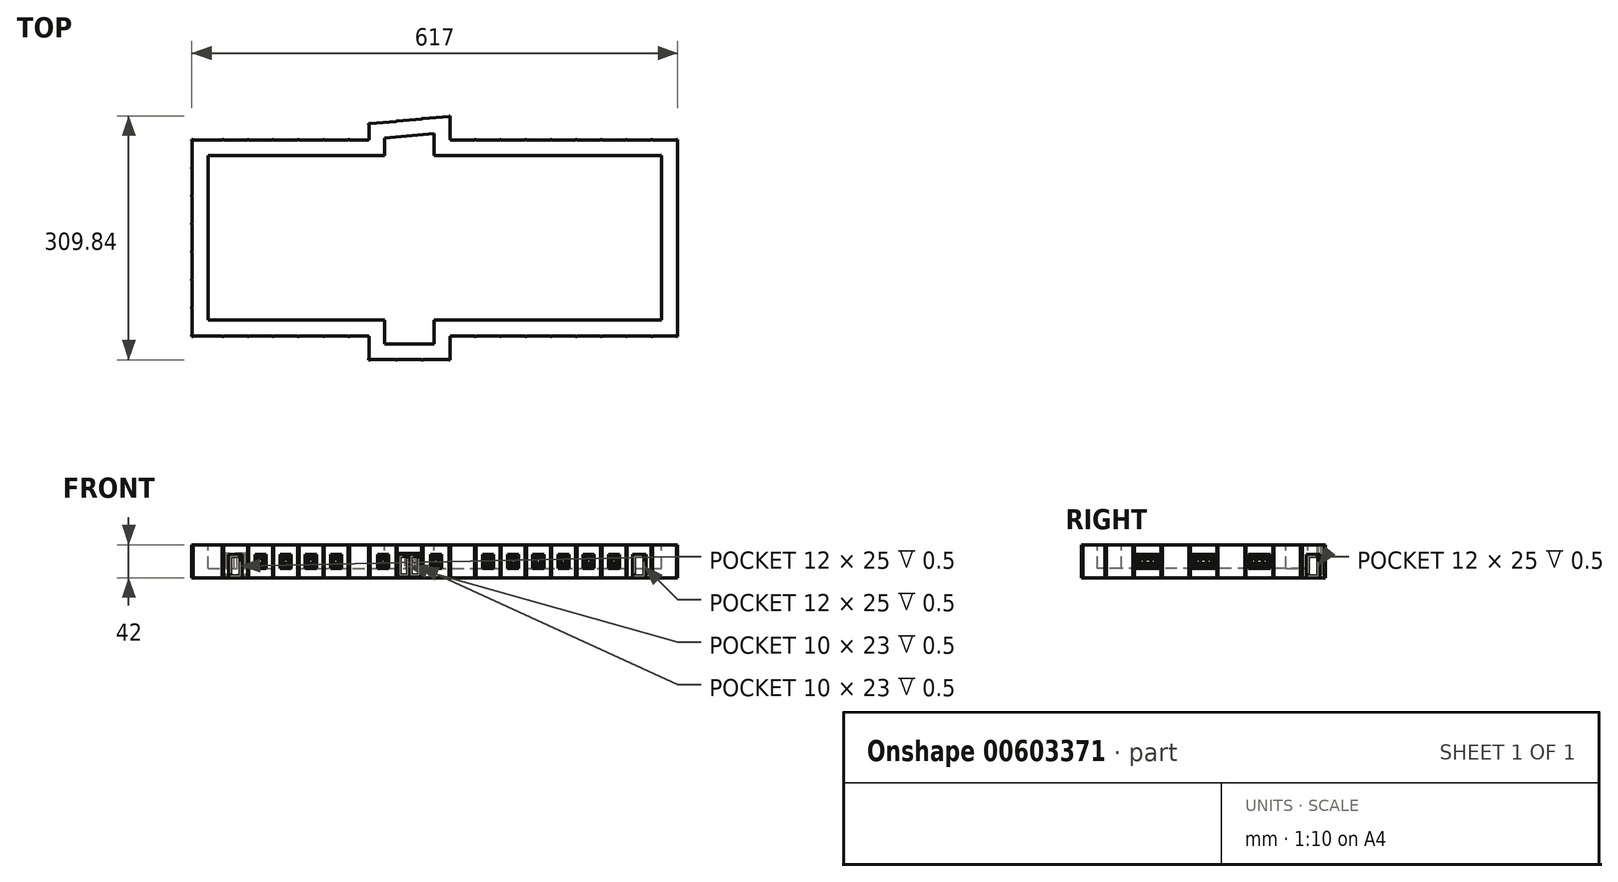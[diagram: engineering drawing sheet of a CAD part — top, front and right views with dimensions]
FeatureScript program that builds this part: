
annotation { "Feature Type Name" : "Feature", "Feature Type Description" : "" }
export const myFeature = defineFeature(function(context is Context, id is Id, definition is map)
    precondition{}
    {
        {
            var Q0;
            Q0=qCreatedBy(makeId("Top.planeOp"),FACE);
            var sketch = newSketch(context, id + "F0", { "sketchPlane" : qUnion([Q0])});
            skLineSegment(sketch, "E0", {"start": v(-327.3, -140.86) * mm, "end": v(-102.6, -140.86) * mm});
            skLineSegment(sketch, "E1", {"start": v(-102.6, -140.86) * mm, "end": v(-102.6, -170.86) * mm});
            skLineSegment(sketch, "E2", {"start": v(-102.6, -170.86) * mm, "end": v(0, -170.86) * mm});
            skLineSegment(sketch, "E3", {"start": v(0, -170.86) * mm, "end": v(0, -140.86) * mm});
            skLineSegment(sketch, "E4", {"start": v(0, -140.86) * mm, "end": v(288.9, -140.86) * mm});
            skLineSegment(sketch, "E5", {"start": v(288.9, -140.86) * mm, "end": v(288.9, 108.14) * mm});
            skLineSegment(sketch, "E6", {"start": v(288.9, 108.14) * mm, "end": v(0, 108.14) * mm});
            skLineSegment(sketch, "E7", {"start": v(0, 108.14) * mm, "end": v(0, 138.14) * mm});
            skLineSegment(sketch, "E8", {"start": v(-102.6, 128.64) * mm, "end": v(-102.6, 108.14) * mm});
            skLineSegment(sketch, "E9", {"start": v(-102.6, 108.14) * mm, "end": v(-327.3, 108.14) * mm});
            skLineSegment(sketch, "E10", {"start": v(-327.3, 108.14) * mm, "end": v(-327.3, -140.86) * mm});
            skLineSegment(sketch, "E11", {"start": v(-102.6, 128.64) * mm, "end": v(0, 138.14) * mm});
            skSolve(sketch);
        }
        {
            var Q0;
            Q0=makeQuery(id+"F0.imprint","IMPRINT",FACE,{"disambiguationData":[TD([[makeQuery(id+"F0.imprint","IMPRINT",EDGE,{"derivedFrom":sQuery(id+"F0.wireOp",EDGE,"E0")}),1.0]])]});
            extrude(context, id + "F1", {"entities" : qUnion([Q0]), "depth" : 42 * mm, "offsetDistance" : 25 * mm});
        }
        {
            var Q0;
            Q0=makeQuery(id+"F19.boolean.opBoolean","MERGE",FACE,{"derivedFrom":[makeQuery(id+"F18.boolean.opBoolean","MERGE",FACE,{"derivedFrom":[makeQuery(id+"F17.boolean.opBoolean","MERGE",FACE,{"derivedFrom":[makeQuery(id+"F16.boolean.opBoolean","MERGE",FACE,{"derivedFrom":[makeQuery(id+"F1.opExtrude","CAP_FACE",FACE,{"disambiguationData":[OSD([sQuery(id+"F0.wireOp",EDGE,"E0"),sQuery(id+"F0.wireOp",EDGE,"E1"),sQuery(id+"F0.wireOp",EDGE,"E2"),sQuery(id+"F0.wireOp",EDGE,"E3"),sQuery(id+"F0.wireOp",EDGE,"E4"),sQuery(id+"F0.wireOp",EDGE,"E5"),sQuery(id+"F0.wireOp",EDGE,"E6"),sQuery(id+"F0.wireOp",EDGE,"E7"),sQuery(id+"F0.wireOp",EDGE,"E8"),sQuery(id+"F0.wireOp",EDGE,"E9"),sQuery(id+"F0.wireOp",EDGE,"E10"),sQuery(id+"F0.wireOp",EDGE,"E11")])],"isStart":false}),makeQuery(id+"F16.opExtrude","SWEPT_FACE",FACE,{"disambiguationData":[OSD([sQuery(id+"F4.wireOp",EDGE,"E25.bottom")])]}),makeQuery(id+"F16.opExtrude","SWEPT_FACE",FACE,{"disambiguationData":[OSD([sQuery(id+"F4.wireOp",EDGE,"E26.bottom")])]}),makeQuery(id+"F16.opExtrude","SWEPT_FACE",FACE,{"disambiguationData":[OSD([sQuery(id+"F4.wireOp",EDGE,"E27.bottom")])]}),makeQuery(id+"F16.opExtrude","SWEPT_FACE",FACE,{"disambiguationData":[OSD([sQuery(id+"F4.wireOp",EDGE,"E28.bottom")])]}),makeQuery(id+"F16.opExtrude","SWEPT_FACE",FACE,{"disambiguationData":[OSD([sQuery(id+"F4.wireOp",EDGE,"E29.bottom")])]}),makeQuery(id+"F16.opExtrude","SWEPT_FACE",FACE,{"disambiguationData":[OSD([sQuery(id+"F4.wireOp",EDGE,"E30.bottom")])]}),makeQuery(id+"F16.opExtrude","SWEPT_FACE",FACE,{"disambiguationData":[OSD([sQuery(id+"F4.wireOp",EDGE,"E31.bottom")])]}),makeQuery(id+"F16.opExtrude","SWEPT_FACE",FACE,{"disambiguationData":[OSD([sQuery(id+"F4.wireOp",EDGE,"E33.bottom")])]}),makeQuery(id+"F16.opExtrude","SWEPT_FACE",FACE,{"disambiguationData":[OSD([sQuery(id+"F6.wireOp",EDGE,"E39.bottom")])]}),makeQuery(id+"F16.opExtrude","SWEPT_FACE",FACE,{"disambiguationData":[OSD([sQuery(id+"F6.wireOp",EDGE,"E40.bottom")])]}),makeQuery(id+"F16.opExtrude","SWEPT_FACE",FACE,{"disambiguationData":[OSD([sQuery(id+"F6.wireOp",EDGE,"E46.bottom")])]}),makeQuery(id+"F16.opExtrude","SWEPT_FACE",FACE,{"disambiguationData":[OSD([sQuery(id+"F6.wireOp",EDGE,"E47.bottom")])]}),makeQuery(id+"F16.opExtrude","SWEPT_FACE",FACE,{"disambiguationData":[OSD([sQuery(id+"F8.wireOp",EDGE,"E52.bottom")])]}),makeQuery(id+"F16.opExtrude","SWEPT_FACE",FACE,{"disambiguationData":[OSD([sQuery(id+"F8.wireOp",EDGE,"E62.bottom")])]}),makeQuery(id+"F16.opExtrude","SWEPT_FACE",FACE,{"disambiguationData":[OSD([sQuery(id+"F8.wireOp",EDGE,"E63.1.0.1")])]}),makeQuery(id+"F16.opExtrude","SWEPT_FACE",FACE,{"disambiguationData":[OSD([sQuery(id+"F8.wireOp",EDGE,"E63.2.0.1")])]}),makeQuery(id+"F16.opExtrude","SWEPT_FACE",FACE,{"disambiguationData":[OSD([sQuery(id+"F8.wireOp",EDGE,"E63.3.0.1")])]}),makeQuery(id+"F16.opExtrude","SWEPT_FACE",FACE,{"disambiguationData":[OSD([sQuery(id+"F8.wireOp",EDGE,"E63.4.0.1")])]}),makeQuery(id+"F16.opExtrude","SWEPT_FACE",FACE,{"disambiguationData":[OSD([sQuery(id+"F8.wireOp",EDGE,"E63.5.0.1")])]}),makeQuery(id+"F16.opExtrude","SWEPT_FACE",FACE,{"disambiguationData":[OSD([sQuery(id+"F8.wireOp",EDGE,"E63.6.0.1")])]}),makeQuery(id+"F16.opExtrude","SWEPT_FACE",FACE,{"disambiguationData":[OSD([sQuery(id+"F8.wireOp",EDGE,"E63.7.0.1")])]}),makeQuery(id+"F16.opExtrude","SWEPT_FACE",FACE,{"disambiguationData":[OSD([sQuery(id+"F8.wireOp",EDGE,"E64.bottom")])]})]}),makeQuery(id+"F17.opExtrude","SWEPT_FACE",FACE,{"disambiguationData":[OSD([sQuery(id+"F5.wireOp",EDGE,"E34.bottom")])]}),makeQuery(id+"F17.opExtrude","SWEPT_FACE",FACE,{"disambiguationData":[OSD([sQuery(id+"F5.wireOp",EDGE,"E36.bottom")])]}),makeQuery(id+"F17.opExtrude","SWEPT_FACE",FACE,{"disambiguationData":[OSD([sQuery(id+"F10.wireOp",EDGE,"E70.bottom")])]}),makeQuery(id+"F17.opExtrude","SWEPT_FACE",FACE,{"disambiguationData":[OSD([sQuery(id+"F10.wireOp",EDGE,"E71.1.0.1")])]}),makeQuery(id+"F17.opExtrude","SWEPT_FACE",FACE,{"disambiguationData":[OSD([sQuery(id+"F10.wireOp",EDGE,"E71.2.0.1")])]}),makeQuery(id+"F17.opExtrude","SWEPT_FACE",FACE,{"disambiguationData":[OSD([sQuery(id+"F10.wireOp",EDGE,"E71.3.0.1")])]}),makeQuery(id+"F17.opExtrude","SWEPT_FACE",FACE,{"disambiguationData":[OSD([sQuery(id+"F10.wireOp",EDGE,"E71.4.0.1")])]}),makeQuery(id+"F17.opExtrude","SWEPT_FACE",FACE,{"disambiguationData":[OSD([sQuery(id+"F10.wireOp",EDGE,"E71.5.0.1")])]}),makeQuery(id+"F17.opExtrude","SWEPT_FACE",FACE,{"disambiguationData":[OSD([sQuery(id+"F10.wireOp",EDGE,"E71.6.0.1")])]}),makeQuery(id+"F17.opExtrude","SWEPT_FACE",FACE,{"disambiguationData":[OSD([sQuery(id+"F10.wireOp",EDGE,"E71.7.0.1")])]}),makeQuery(id+"F17.opExtrude","SWEPT_FACE",FACE,{"disambiguationData":[OSD([sQuery(id+"F10.wireOp",EDGE,"E71.8.0.1")])]}),makeQuery(id+"F17.opExtrude","SWEPT_FACE",FACE,{"disambiguationData":[OSD([sQuery(id+"F12.wireOp",EDGE,"E93.bottom")])]}),makeQuery(id+"F17.opExtrude","SWEPT_FACE",FACE,{"disambiguationData":[OSD([sQuery(id+"F12.wireOp",EDGE,"E95.bottom")])]})]}),makeQuery(id+"F18.opExtrude","SWEPT_FACE",FACE,{"disambiguationData":[OSD([sQuery(id+"F7.wireOp",EDGE,"E48.bottom")])]}),makeQuery(id+"F18.opExtrude","SWEPT_FACE",FACE,{"disambiguationData":[OSD([sQuery(id+"F7.wireOp",EDGE,"E50.bottom")])]}),makeQuery(id+"F18.opExtrude","SWEPT_FACE",FACE,{"disambiguationData":[OSD([sQuery(id+"F9.wireOp",EDGE,"E66.bottom")])]}),makeQuery(id+"F18.opExtrude","SWEPT_FACE",FACE,{"disambiguationData":[OSD([sQuery(id+"F9.wireOp",EDGE,"E67.1.0.1")])]}),makeQuery(id+"F18.opExtrude","SWEPT_FACE",FACE,{"disambiguationData":[OSD([sQuery(id+"F9.wireOp",EDGE,"E67.2.0.1")])]}),makeQuery(id+"F18.opExtrude","SWEPT_FACE",FACE,{"disambiguationData":[OSD([sQuery(id+"F9.wireOp",EDGE,"E67.3.0.1")])]}),makeQuery(id+"F18.opExtrude","SWEPT_FACE",FACE,{"disambiguationData":[OSD([sQuery(id+"F9.wireOp",EDGE,"E67.4.0.1")])]}),makeQuery(id+"F18.opExtrude","SWEPT_FACE",FACE,{"disambiguationData":[OSD([sQuery(id+"F9.wireOp",EDGE,"E67.5.0.1")])]}),makeQuery(id+"F18.opExtrude","SWEPT_FACE",FACE,{"disambiguationData":[OSD([sQuery(id+"F9.wireOp",EDGE,"E67.6.0.1")])]}),makeQuery(id+"F18.opExtrude","SWEPT_FACE",FACE,{"disambiguationData":[OSD([sQuery(id+"F9.wireOp",EDGE,"E67.7.0.1")])]}),makeQuery(id+"F18.opExtrude","SWEPT_FACE",FACE,{"disambiguationData":[OSD([sQuery(id+"F9.wireOp",EDGE,"E67.8.0.1")])]}),makeQuery(id+"F18.opExtrude","SWEPT_FACE",FACE,{"disambiguationData":[OSD([sQuery(id+"F14.wireOp",EDGE,"E107.bottom")])]}),makeQuery(id+"F18.opExtrude","SWEPT_FACE",FACE,{"disambiguationData":[OSD([sQuery(id+"F14.wireOp",EDGE,"E109.bottom")])]})]}),makeQuery(id+"F19.opExtrude","SWEPT_FACE",FACE,{"disambiguationData":[OSD([sQuery(id+"F11.wireOp",EDGE,"E84.top")])]}),makeQuery(id+"F19.opExtrude","SWEPT_FACE",FACE,{"disambiguationData":[OSD([sQuery(id+"F11.wireOp",EDGE,"E85.top")])]}),makeQuery(id+"F19.opExtrude","SWEPT_FACE",FACE,{"disambiguationData":[OSD([sQuery(id+"F11.wireOp",EDGE,"E86.top")])]}),makeQuery(id+"F19.opExtrude","SWEPT_FACE",FACE,{"disambiguationData":[OSD([sQuery(id+"F11.wireOp",EDGE,"E87.top")])]}),makeQuery(id+"F19.opExtrude","SWEPT_FACE",FACE,{"disambiguationData":[OSD([sQuery(id+"F11.wireOp",EDGE,"E88.top")])]}),makeQuery(id+"F19.opExtrude","SWEPT_FACE",FACE,{"disambiguationData":[OSD([sQuery(id+"F11.wireOp",EDGE,"E89.top")])]}),makeQuery(id+"F19.opExtrude","SWEPT_FACE",FACE,{"disambiguationData":[OSD([sQuery(id+"F11.wireOp",EDGE,"E90.top")])]}),makeQuery(id+"F19.opExtrude","SWEPT_FACE",FACE,{"disambiguationData":[OSD([sQuery(id+"F11.wireOp",EDGE,"E92.top")])]}),makeQuery(id+"F19.opExtrude","SWEPT_FACE",FACE,{"disambiguationData":[OSD([sQuery(id+"F13.wireOp",EDGE,"E98.bottom")])]}),makeQuery(id+"F19.opExtrude","SWEPT_FACE",FACE,{"disambiguationData":[OSD([sQuery(id+"F13.wireOp",EDGE,"E99.bottom")])]}),makeQuery(id+"F19.opExtrude","SWEPT_FACE",FACE,{"disambiguationData":[OSD([sQuery(id+"F13.wireOp",EDGE,"E105.bottom")])]}),makeQuery(id+"F19.opExtrude","SWEPT_FACE",FACE,{"disambiguationData":[OSD([sQuery(id+"F13.wireOp",EDGE,"E106.bottom")])]}),makeQuery(id+"F19.opExtrude","SWEPT_FACE",FACE,{"disambiguationData":[OSD([sQuery(id+"F15.wireOp",EDGE,"E111.top")])]}),makeQuery(id+"F19.opExtrude","SWEPT_FACE",FACE,{"disambiguationData":[OSD([sQuery(id+"F15.wireOp",EDGE,"E121.top")])]}),makeQuery(id+"F19.opExtrude","SWEPT_FACE",FACE,{"disambiguationData":[OSD([sQuery(id+"F15.wireOp",EDGE,"E122.1.0.3")])]}),makeQuery(id+"F19.opExtrude","SWEPT_FACE",FACE,{"disambiguationData":[OSD([sQuery(id+"F15.wireOp",EDGE,"E122.2.0.3")])]}),makeQuery(id+"F19.opExtrude","SWEPT_FACE",FACE,{"disambiguationData":[OSD([sQuery(id+"F15.wireOp",EDGE,"E122.3.0.3")])]}),makeQuery(id+"F19.opExtrude","SWEPT_FACE",FACE,{"disambiguationData":[OSD([sQuery(id+"F15.wireOp",EDGE,"E122.4.0.3")])]}),makeQuery(id+"F19.opExtrude","SWEPT_FACE",FACE,{"disambiguationData":[OSD([sQuery(id+"F15.wireOp",EDGE,"E122.5.0.3")])]}),makeQuery(id+"F19.opExtrude","SWEPT_FACE",FACE,{"disambiguationData":[OSD([sQuery(id+"F15.wireOp",EDGE,"E122.6.0.3")])]}),makeQuery(id+"F19.opExtrude","SWEPT_FACE",FACE,{"disambiguationData":[OSD([sQuery(id+"F15.wireOp",EDGE,"E122.7.0.3")])]}),makeQuery(id+"F19.opExtrude","SWEPT_FACE",FACE,{"disambiguationData":[OSD([sQuery(id+"F15.wireOp",EDGE,"E123.top")])]})]});
            var sketch = newSketch(context, id + "F2", { "sketchPlane" : qUnion([Q0])});
            skLineSegment(sketch, "E12.0", {"start": v(-20, 116.2) * mm, "end": v(-82.6, 110.4) * mm});
            skLineSegment(sketch, "E12.1", {"start": v(-82.6, -120.86) * mm, "end": v(-82.6, -150.86) * mm});
            skLineSegment(sketch, "E12.2", {"start": v(-307.3, -120.86) * mm, "end": v(-82.6, -120.86) * mm});
            skLineSegment(sketch, "E12.3", {"start": v(-307.3, 88.14) * mm, "end": v(-307.3, -120.86) * mm});
            skLineSegment(sketch, "E12.4", {"start": v(-82.6, 88.14) * mm, "end": v(-307.3, 88.14) * mm});
            skLineSegment(sketch, "E12.5", {"start": v(-82.6, -150.86) * mm, "end": v(-20, -150.86) * mm});
            skLineSegment(sketch, "E12.6", {"start": v(-82.6, 110.4) * mm, "end": v(-82.6, 88.14) * mm});
            skLineSegment(sketch, "E12.7", {"start": v(-20, -150.86) * mm, "end": v(-20, -120.86) * mm});
            skLineSegment(sketch, "E12.8", {"start": v(-20, -120.86) * mm, "end": v(268.9, -120.86) * mm});
            skLineSegment(sketch, "E12.9", {"start": v(268.9, -120.86) * mm, "end": v(268.9, 88.14) * mm});
            skLineSegment(sketch, "E12.10", {"start": v(268.9, 88.14) * mm, "end": v(-20, 88.14) * mm});
            skLineSegment(sketch, "E12.11", {"start": v(-20, 88.14) * mm, "end": v(-20, 116.2) * mm});
            skSolve(sketch);
        }
        {
            var Q0;
            Q0=makeQuery(id+"F2.imprint","IMPRINT",FACE,{"disambiguationData":[TD([[makeQuery(id+"F2.imprint","IMPRINT",EDGE,{"derivedFrom":sQuery(id+"F2.wireOp",EDGE,"E12.0")}),1.0]])]});
            extrude(context, id + "F3", {"entities" : qUnion([Q0]), "operationType" : NewBodyOperationType.REMOVE, "oppositeDirection" : true, "depth" : 30 * mm, "offsetDistance" : 25 * mm});
        }
        {
            var Q0;
            Q0=makeQuery(id+"F1.opExtrude","SWEPT_FACE",FACE,{"disambiguationData":[OSD([sQuery(id+"F0.wireOp",EDGE,"E0")])]});
            var sketch = newSketch(context, id + "F4", { "sketchPlane" : qUnion([Q0])});
            skPoint(sketch, "E13", {"position": v(-288.38, 0) * mm});
            skPoint(sketch, "E14", {"position": v(-256.38, 0) * mm});
            skPoint(sketch, "E15", {"position": v(-224.38, 0) * mm});
            skPoint(sketch, "E16", {"position": v(-192.38, 0) * mm});
            skPoint(sketch, "E17", {"position": v(-160.38, 0) * mm});
            skPoint(sketch, "E18", {"position": v(-128.38, 0) * mm});
            skLineSegment(sketch, "E19", {"start": v(-288.38, 42) * mm, "end": v(-288.38, -18.35) * mm, "construction": true});
            skLineSegment(sketch, "E20", {"start": v(-256.38, 42) * mm, "end": v(-256.38, 0) * mm, "construction": true});
            skLineSegment(sketch, "E21", {"start": v(-224.38, 42) * mm, "end": v(-224.38, 0) * mm, "construction": true});
            skLineSegment(sketch, "E22", {"start": v(-192.38, 42) * mm, "end": v(-192.38, 0) * mm, "construction": true});
            skLineSegment(sketch, "E23", {"start": v(-160.38, 42) * mm, "end": v(-160.38, 0) * mm, "construction": true});
            skLineSegment(sketch, "E24", {"start": v(-128.38, 42) * mm, "end": v(-128.38, 0) * mm, "construction": true});
            skLineSegment(sketch, "E25.bottom", {"start": v(-289.18, 42) * mm, "end": v(-287.58, 42) * mm});
            skLineSegment(sketch, "E25.top", {"start": v(-289.18, 0) * mm, "end": v(-287.58, 0) * mm});
            skLineSegment(sketch, "E25.left", {"start": v(-289.18, 42) * mm, "end": v(-289.18, 0) * mm});
            skLineSegment(sketch, "E25.right", {"start": v(-287.58, 42) * mm, "end": v(-287.58, 0) * mm});
            skLineSegment(sketch, "E26.bottom", {"start": v(-257.18, 42) * mm, "end": v(-255.57, 42) * mm});
            skLineSegment(sketch, "E26.top", {"start": v(-257.18, 0) * mm, "end": v(-255.57, 0) * mm});
            skLineSegment(sketch, "E26.left", {"start": v(-257.18, 42) * mm, "end": v(-257.18, 0) * mm});
            skLineSegment(sketch, "E26.right", {"start": v(-255.57, 42) * mm, "end": v(-255.57, 0) * mm});
            skLineSegment(sketch, "E27.bottom", {"start": v(-225.18, 42) * mm, "end": v(-223.58, 42) * mm});
            skLineSegment(sketch, "E27.top", {"start": v(-225.18, 0) * mm, "end": v(-223.57, 0) * mm});
            skLineSegment(sketch, "E27.left", {"start": v(-225.18, 42) * mm, "end": v(-225.18, 0) * mm});
            skLineSegment(sketch, "E27.right", {"start": v(-223.58, 42) * mm, "end": v(-223.58, 0) * mm});
            skLineSegment(sketch, "E28.bottom", {"start": v(-193.18, 42) * mm, "end": v(-191.58, 42) * mm});
            skLineSegment(sketch, "E28.top", {"start": v(-193.18, 0) * mm, "end": v(-191.57, 0) * mm});
            skLineSegment(sketch, "E28.left", {"start": v(-193.18, 42) * mm, "end": v(-193.18, 0) * mm});
            skLineSegment(sketch, "E28.right", {"start": v(-191.58, 42) * mm, "end": v(-191.58, 0) * mm});
            skLineSegment(sketch, "E29.bottom", {"start": v(-161.18, 42) * mm, "end": v(-159.58, 42) * mm});
            skLineSegment(sketch, "E29.top", {"start": v(-161.18, 0) * mm, "end": v(-159.58, 0) * mm});
            skLineSegment(sketch, "E29.left", {"start": v(-161.18, 42) * mm, "end": v(-161.18, 0) * mm});
            skLineSegment(sketch, "E29.right", {"start": v(-159.58, 42) * mm, "end": v(-159.58, 0) * mm});
            skLineSegment(sketch, "E30.bottom", {"start": v(-129.18, 42) * mm, "end": v(-127.58, 42) * mm});
            skLineSegment(sketch, "E30.top", {"start": v(-129.18, 0) * mm, "end": v(-127.58, 0) * mm});
            skLineSegment(sketch, "E30.left", {"start": v(-129.18, 42) * mm, "end": v(-129.18, 0) * mm});
            skLineSegment(sketch, "E30.right", {"start": v(-127.58, 42) * mm, "end": v(-127.58, 0) * mm});
            skLineSegment(sketch, "E31.bottom", {"start": v(-102.6, 42) * mm, "end": v(-103.4, 42) * mm});
            skLineSegment(sketch, "E31.top", {"start": v(-102.6, 0) * mm, "end": v(-103.4, 0) * mm});
            skLineSegment(sketch, "E31.left", {"start": v(-102.6, 42) * mm, "end": v(-102.6, 0) * mm});
            skLineSegment(sketch, "E31.right", {"start": v(-103.4, 42) * mm, "end": v(-103.4, 0) * mm});
            skPoint(sketch, "E32", {"position": v(-326.1, 42) * mm});
            skLineSegment(sketch, "E33.bottom", {"start": v(-326.1, 42) * mm, "end": v(-327.7, 42) * mm});
            skLineSegment(sketch, "E33.top", {"start": v(-326.1, 0) * mm, "end": v(-327.7, 0) * mm});
            skLineSegment(sketch, "E33.left", {"start": v(-326.1, 42) * mm, "end": v(-326.1, 0) * mm});
            skLineSegment(sketch, "E33.right", {"start": v(-327.7, 42) * mm, "end": v(-327.7, 0) * mm});
            skSolve(sketch);
        }
        {
            var Q0;
            Q0=makeQuery(id+"F1.opExtrude","SWEPT_FACE",FACE,{"disambiguationData":[OSD([sQuery(id+"F0.wireOp",EDGE,"E1")])]});
            var sketch = newSketch(context, id + "F5", { "sketchPlane" : qUnion([Q0])});
            skLineSegment(sketch, "E34.bottom", {"start": v(140.86, 42) * mm, "end": v(141.66, 42) * mm});
            skLineSegment(sketch, "E34.top", {"start": v(140.86, 0) * mm, "end": v(141.66, 0) * mm});
            skLineSegment(sketch, "E34.left", {"start": v(140.86, 42) * mm, "end": v(140.86, 0) * mm});
            skLineSegment(sketch, "E34.right", {"start": v(141.66, 42) * mm, "end": v(141.66, 0) * mm});
            skPoint(sketch, "E35", {"position": v(169.66, 42) * mm});
            skLineSegment(sketch, "E36.bottom", {"start": v(169.66, 42) * mm, "end": v(171.26, 42) * mm});
            skLineSegment(sketch, "E36.top", {"start": v(169.66, 0) * mm, "end": v(171.26, 0) * mm});
            skLineSegment(sketch, "E36.left", {"start": v(169.66, 42) * mm, "end": v(169.66, 0) * mm});
            skLineSegment(sketch, "E36.right", {"start": v(171.26, 42) * mm, "end": v(171.26, 0) * mm});
            skSolve(sketch);
        }
        {
            var Q0;
            Q0=makeQuery(id+"F1.opExtrude","SWEPT_FACE",FACE,{"disambiguationData":[OSD([sQuery(id+"F0.wireOp",EDGE,"E2")])]});
            var sketch = newSketch(context, id + "F6", { "sketchPlane" : qUnion([Q0])});
            skPoint(sketch, "E37", {"position": v(-101.4, 42) * mm});
            skPoint(sketch, "E38", {"position": v(-1.2, 42) * mm});
            skLineSegment(sketch, "E39.bottom", {"start": v(-101.4, 42) * mm, "end": v(-103, 42) * mm});
            skLineSegment(sketch, "E39.top", {"start": v(-101.4, 0) * mm, "end": v(-103, 0) * mm});
            skLineSegment(sketch, "E39.left", {"start": v(-101.4, 42) * mm, "end": v(-101.4, 0) * mm});
            skLineSegment(sketch, "E39.right", {"start": v(-103, 42) * mm, "end": v(-103, 0) * mm});
            skLineSegment(sketch, "E40.bottom", {"start": v(-1.2, 42) * mm, "end": v(0.4, 42) * mm});
            skLineSegment(sketch, "E40.top", {"start": v(-1.2, 0) * mm, "end": v(0.4, 0) * mm});
            skLineSegment(sketch, "E40.left", {"start": v(-1.2, 42) * mm, "end": v(-1.2, 0) * mm});
            skLineSegment(sketch, "E40.right", {"start": v(0.4, 42) * mm, "end": v(0.4, 0) * mm});
            skPoint(sketch, "E41", {"position": v(-51.3, 42) * mm});
            skPoint(sketch, "E42", {"position": v(-51.3, 0) * mm});
            skLineSegment(sketch, "E43", {"start": v(-51.3, 42) * mm, "end": v(-51.3, 0) * mm, "construction": true});
            skPoint(sketch, "E44", {"position": v(-67.8, 42) * mm});
            skPoint(sketch, "E45", {"position": v(-34.8, 42) * mm});
            skLineSegment(sketch, "E46.bottom", {"start": v(-35.6, 42) * mm, "end": v(-34, 42) * mm});
            skLineSegment(sketch, "E46.top", {"start": v(-35.6, 0) * mm, "end": v(-34, 0) * mm});
            skLineSegment(sketch, "E46.left", {"start": v(-35.6, 42) * mm, "end": v(-35.6, 0) * mm});
            skLineSegment(sketch, "E46.right", {"start": v(-34, 42) * mm, "end": v(-34, 0) * mm});
            skLineSegment(sketch, "E47.bottom", {"start": v(-68.6, 42) * mm, "end": v(-67, 42) * mm});
            skLineSegment(sketch, "E47.top", {"start": v(-68.6, 0) * mm, "end": v(-67, 0) * mm});
            skLineSegment(sketch, "E47.left", {"start": v(-68.6, 42) * mm, "end": v(-68.6, 0) * mm});
            skLineSegment(sketch, "E47.right", {"start": v(-67, 42) * mm, "end": v(-67, 0) * mm});
            skSolve(sketch);
        }
        {
            var Q0;
            Q0=makeQuery(id+"F1.opExtrude","SWEPT_FACE",FACE,{"disambiguationData":[OSD([sQuery(id+"F0.wireOp",EDGE,"E3")])]});
            var sketch = newSketch(context, id + "F7", { "sketchPlane" : qUnion([Q0])});
            skLineSegment(sketch, "E48.bottom", {"start": v(-140.86, 42) * mm, "end": v(-141.66, 42) * mm});
            skLineSegment(sketch, "E48.top", {"start": v(-140.86, 0) * mm, "end": v(-141.66, 0) * mm});
            skLineSegment(sketch, "E48.left", {"start": v(-140.86, 42) * mm, "end": v(-140.86, 0) * mm});
            skLineSegment(sketch, "E48.right", {"start": v(-141.66, 42) * mm, "end": v(-141.66, 0) * mm});
            skPoint(sketch, "E49", {"position": v(-169.66, 42) * mm});
            skLineSegment(sketch, "E50.bottom", {"start": v(-169.66, 42) * mm, "end": v(-171.26, 42) * mm});
            skLineSegment(sketch, "E50.top", {"start": v(-169.66, 0) * mm, "end": v(-171.26, 0) * mm});
            skLineSegment(sketch, "E50.left", {"start": v(-169.66, 42) * mm, "end": v(-169.66, 0) * mm});
            skLineSegment(sketch, "E50.right", {"start": v(-171.26, 42) * mm, "end": v(-171.26, 0) * mm});
            skSolve(sketch);
        }
        {
            var Q0;
            Q0=makeQuery(id+"F1.opExtrude","SWEPT_FACE",FACE,{"disambiguationData":[OSD([sQuery(id+"F0.wireOp",EDGE,"E4")])]});
            var sketch = newSketch(context, id + "F8", { "sketchPlane" : qUnion([Q0])});
            skPoint(sketch, "E51", {"position": v(287.7, 42) * mm});
            skLineSegment(sketch, "E52.bottom", {"start": v(287.7, 42) * mm, "end": v(289.3, 42) * mm});
            skLineSegment(sketch, "E52.top", {"start": v(287.7, 0) * mm, "end": v(289.3, 0) * mm});
            skLineSegment(sketch, "E52.left", {"start": v(287.7, 42) * mm, "end": v(287.7, 0) * mm});
            skLineSegment(sketch, "E52.right", {"start": v(289.3, 42) * mm, "end": v(289.3, 0) * mm});
            skPoint(sketch, "E53", {"position": v(288.5, 42) * mm});
            skPoint(sketch, "E54", {"position": v(256.5, 42) * mm});
            skPoint(sketch, "E55", {"position": v(224.5, 42) * mm});
            skPoint(sketch, "E56", {"position": v(192.5, 42) * mm});
            skPoint(sketch, "E57", {"position": v(160.5, 42) * mm});
            skPoint(sketch, "E58", {"position": v(128.5, 42) * mm});
            skPoint(sketch, "E59", {"position": v(96.5, 42) * mm});
            skPoint(sketch, "E60", {"position": v(64.5, 42) * mm});
            skPoint(sketch, "E61", {"position": v(32.5, 42) * mm});
            skLineSegment(sketch, "E62.bottom", {"start": v(255.7, 42) * mm, "end": v(257.3, 42) * mm});
            skLineSegment(sketch, "E62.top", {"start": v(255.7, 0) * mm, "end": v(257.3, 0) * mm});
            skLineSegment(sketch, "E62.left", {"start": v(255.7, 42) * mm, "end": v(255.7, 0) * mm});
            skLineSegment(sketch, "E62.right", {"start": v(257.3, 42) * mm, "end": v(257.3, 0) * mm});
            skLineSegment(sketch, "E63.1.0.0", {"start": v(223.7, 42) * mm, "end": v(223.7, 0) * mm});
            skLineSegment(sketch, "E63.1.0.1", {"start": v(223.7, 42) * mm, "end": v(225.3, 42) * mm});
            skLineSegment(sketch, "E63.1.0.2", {"start": v(225.3, 42) * mm, "end": v(225.3, 0) * mm});
            skLineSegment(sketch, "E63.1.0.3", {"start": v(223.7, 0) * mm, "end": v(225.3, 0) * mm});
            skLineSegment(sketch, "E63.2.0.0", {"start": v(191.7, 42) * mm, "end": v(191.7, 0) * mm});
            skLineSegment(sketch, "E63.2.0.1", {"start": v(191.7, 42) * mm, "end": v(193.3, 42) * mm});
            skLineSegment(sketch, "E63.2.0.2", {"start": v(193.3, 42) * mm, "end": v(193.3, 0) * mm});
            skLineSegment(sketch, "E63.2.0.3", {"start": v(191.7, 0) * mm, "end": v(193.3, 0) * mm});
            skLineSegment(sketch, "E63.3.0.0", {"start": v(159.7, 42) * mm, "end": v(159.7, 0) * mm});
            skLineSegment(sketch, "E63.3.0.1", {"start": v(159.7, 42) * mm, "end": v(161.3, 42) * mm});
            skLineSegment(sketch, "E63.3.0.2", {"start": v(161.3, 42) * mm, "end": v(161.3, 0) * mm});
            skLineSegment(sketch, "E63.3.0.3", {"start": v(159.7, 0) * mm, "end": v(161.3, 0) * mm});
            skLineSegment(sketch, "E63.4.0.0", {"start": v(127.7, 42) * mm, "end": v(127.7, 0) * mm});
            skLineSegment(sketch, "E63.4.0.1", {"start": v(127.7, 42) * mm, "end": v(129.3, 42) * mm});
            skLineSegment(sketch, "E63.4.0.2", {"start": v(129.3, 42) * mm, "end": v(129.3, 0) * mm});
            skLineSegment(sketch, "E63.4.0.3", {"start": v(127.7, 0) * mm, "end": v(129.3, 0) * mm});
            skLineSegment(sketch, "E63.5.0.0", {"start": v(95.7, 42) * mm, "end": v(95.7, 0) * mm});
            skLineSegment(sketch, "E63.5.0.1", {"start": v(95.7, 42) * mm, "end": v(97.3, 42) * mm});
            skLineSegment(sketch, "E63.5.0.2", {"start": v(97.3, 42) * mm, "end": v(97.3, 0) * mm});
            skLineSegment(sketch, "E63.5.0.3", {"start": v(95.7, 0) * mm, "end": v(97.3, 0) * mm});
            skLineSegment(sketch, "E63.6.0.0", {"start": v(63.7, 42) * mm, "end": v(63.7, 0) * mm});
            skLineSegment(sketch, "E63.6.0.1", {"start": v(63.7, 42) * mm, "end": v(65.3, 42) * mm});
            skLineSegment(sketch, "E63.6.0.2", {"start": v(65.3, 42) * mm, "end": v(65.3, 0) * mm});
            skLineSegment(sketch, "E63.6.0.3", {"start": v(63.7, 0) * mm, "end": v(65.3, 0) * mm});
            skLineSegment(sketch, "E63.7.0.0", {"start": v(31.7, 42) * mm, "end": v(31.7, 0) * mm});
            skLineSegment(sketch, "E63.7.0.1", {"start": v(31.7, 42) * mm, "end": v(33.3, 42) * mm});
            skLineSegment(sketch, "E63.7.0.2", {"start": v(33.3, 42) * mm, "end": v(33.3, 0) * mm});
            skLineSegment(sketch, "E63.7.0.3", {"start": v(31.7, 0) * mm, "end": v(33.3, 0) * mm});
            skLineSegment(sketch, "E63.direction1", {"start": v(255.7, 0) * mm, "end": v(223.7, 0) * mm, "construction": true});
            skLineSegment(sketch, "E64.bottom", {"start": v(0, 42) * mm, "end": v(0.8, 42) * mm});
            skLineSegment(sketch, "E64.top", {"start": v(0, 0) * mm, "end": v(0.8, 0) * mm});
            skLineSegment(sketch, "E64.left", {"start": v(0, 42) * mm, "end": v(0, 0) * mm});
            skLineSegment(sketch, "E64.right", {"start": v(0.8, 42) * mm, "end": v(0.8, 0) * mm});
            skSolve(sketch);
        }
        {
            var Q0;
            Q0=makeQuery(id+"F1.opExtrude","SWEPT_FACE",FACE,{"disambiguationData":[OSD([sQuery(id+"F0.wireOp",EDGE,"E5")])]});
            var sketch = newSketch(context, id + "F9", { "sketchPlane" : qUnion([Q0])});
            skPoint(sketch, "E65", {"position": v(-139.66, 42) * mm});
            skLineSegment(sketch, "E66.bottom", {"start": v(-139.66, 42) * mm, "end": v(-141.26, 42) * mm});
            skLineSegment(sketch, "E66.top", {"start": v(-139.66, 0) * mm, "end": v(-141.26, 0) * mm});
            skLineSegment(sketch, "E66.left", {"start": v(-139.66, 42) * mm, "end": v(-139.66, 0) * mm});
            skLineSegment(sketch, "E66.right", {"start": v(-141.26, 42) * mm, "end": v(-141.26, 0) * mm});
            skLineSegment(sketch, "E67.1.0.0", {"start": v(-104.2, 42) * mm, "end": v(-104.2, 0) * mm});
            skLineSegment(sketch, "E67.1.0.1", {"start": v(-104.2, 42) * mm, "end": v(-105.8, 42) * mm});
            skLineSegment(sketch, "E67.1.0.2", {"start": v(-105.8, 42) * mm, "end": v(-105.8, 0) * mm});
            skLineSegment(sketch, "E67.1.0.3", {"start": v(-104.2, 0) * mm, "end": v(-105.8, 0) * mm});
            skLineSegment(sketch, "E67.2.0.0", {"start": v(-68.74, 42) * mm, "end": v(-68.74, 0) * mm});
            skLineSegment(sketch, "E67.2.0.1", {"start": v(-68.74, 42) * mm, "end": v(-70.34, 42) * mm});
            skLineSegment(sketch, "E67.2.0.2", {"start": v(-70.34, 42) * mm, "end": v(-70.34, 0) * mm});
            skLineSegment(sketch, "E67.2.0.3", {"start": v(-68.74, 0) * mm, "end": v(-70.34, 0) * mm});
            skLineSegment(sketch, "E67.3.0.0", {"start": v(-33.29, 42) * mm, "end": v(-33.29, 0) * mm});
            skLineSegment(sketch, "E67.3.0.1", {"start": v(-33.29, 42) * mm, "end": v(-34.89, 42) * mm});
            skLineSegment(sketch, "E67.3.0.2", {"start": v(-34.89, 42) * mm, "end": v(-34.89, 0) * mm});
            skLineSegment(sketch, "E67.3.0.3", {"start": v(-33.29, 0) * mm, "end": v(-34.89, 0) * mm});
            skLineSegment(sketch, "E67.4.0.0", {"start": v(2.17, 42) * mm, "end": v(2.17, 0) * mm});
            skLineSegment(sketch, "E67.4.0.1", {"start": v(2.17, 42) * mm, "end": v(0.57, 42) * mm});
            skLineSegment(sketch, "E67.4.0.2", {"start": v(0.57, 42) * mm, "end": v(0.57, 0) * mm});
            skLineSegment(sketch, "E67.4.0.3", {"start": v(2.17, 0) * mm, "end": v(0.57, 0) * mm});
            skLineSegment(sketch, "E67.5.0.0", {"start": v(37.63, 42) * mm, "end": v(37.63, 0) * mm});
            skLineSegment(sketch, "E67.5.0.1", {"start": v(37.63, 42) * mm, "end": v(36.03, 42) * mm});
            skLineSegment(sketch, "E67.5.0.2", {"start": v(36.03, 42) * mm, "end": v(36.03, 0) * mm});
            skLineSegment(sketch, "E67.5.0.3", {"start": v(37.63, 0) * mm, "end": v(36.03, 0) * mm});
            skLineSegment(sketch, "E67.6.0.0", {"start": v(73.09, 42) * mm, "end": v(73.09, 0) * mm});
            skLineSegment(sketch, "E67.6.0.1", {"start": v(73.09, 42) * mm, "end": v(71.49, 42) * mm});
            skLineSegment(sketch, "E67.6.0.2", {"start": v(71.49, 42) * mm, "end": v(71.49, 0) * mm});
            skLineSegment(sketch, "E67.6.0.3", {"start": v(73.09, 0) * mm, "end": v(71.49, 0) * mm});
            skLineSegment(sketch, "E67.direction1", {"start": v(-139.66, 0) * mm, "end": v(-104.2, 0) * mm, "construction": true});
            skLineSegment(sketch, "E68.0.7.0", {"start": v(108.54, 42) * mm, "end": v(108.54, 0) * mm});
            skLineSegment(sketch, "E68.3.7.0", {"start": v(108.54, 42) * mm, "end": v(106.94, 42) * mm});
            skLineSegment(sketch, "E68.6.7.0", {"start": v(106.94, 42) * mm, "end": v(106.94, 0) * mm});
            skLineSegment(sketch, "E68.9.7.0", {"start": v(108.54, 0) * mm, "end": v(106.94, 0) * mm});
            skSolve(sketch);
        }
        {
            var Q0;
            Q0=makeQuery(id+"F1.opExtrude","SWEPT_FACE",FACE,{"disambiguationData":[OSD([sQuery(id+"F0.wireOp",EDGE,"E10")])]});
            var sketch = newSketch(context, id + "F10", { "sketchPlane" : qUnion([Q0])});
            skPoint(sketch, "E69", {"position": v(-107.24, 42) * mm});
            skLineSegment(sketch, "E70.bottom", {"start": v(-107.24, 42) * mm, "end": v(-108.84, 42) * mm});
            skLineSegment(sketch, "E70.top", {"start": v(-107.24, 0) * mm, "end": v(-108.84, 0) * mm});
            skLineSegment(sketch, "E70.left", {"start": v(-107.24, 42) * mm, "end": v(-107.24, 0) * mm});
            skLineSegment(sketch, "E70.right", {"start": v(-108.84, 42) * mm, "end": v(-108.84, 0) * mm});
            skLineSegment(sketch, "E71.1.0.0", {"start": v(-71.74, 42) * mm, "end": v(-71.74, 0) * mm});
            skLineSegment(sketch, "E71.1.0.1", {"start": v(-71.74, 42) * mm, "end": v(-73.34, 42) * mm});
            skLineSegment(sketch, "E71.1.0.2", {"start": v(-73.34, 42) * mm, "end": v(-73.34, 0) * mm});
            skLineSegment(sketch, "E71.1.0.3", {"start": v(-71.74, 0) * mm, "end": v(-73.34, 0) * mm});
            skLineSegment(sketch, "E71.2.0.0", {"start": v(-36.24, 42) * mm, "end": v(-36.24, 0) * mm});
            skLineSegment(sketch, "E71.2.0.1", {"start": v(-36.24, 42) * mm, "end": v(-37.84, 42) * mm});
            skLineSegment(sketch, "E71.2.0.2", {"start": v(-37.84, 42) * mm, "end": v(-37.84, 0) * mm});
            skLineSegment(sketch, "E71.2.0.3", {"start": v(-36.24, 0) * mm, "end": v(-37.84, 0) * mm});
            skLineSegment(sketch, "E71.3.0.0", {"start": v(-0.74, 42) * mm, "end": v(-0.74, 0) * mm});
            skLineSegment(sketch, "E71.3.0.1", {"start": v(-0.74, 42) * mm, "end": v(-2.34, 42) * mm});
            skLineSegment(sketch, "E71.3.0.2", {"start": v(-2.34, 42) * mm, "end": v(-2.34, 0) * mm});
            skLineSegment(sketch, "E71.3.0.3", {"start": v(-0.74, 0) * mm, "end": v(-2.34, 0) * mm});
            skLineSegment(sketch, "E71.4.0.0", {"start": v(34.76, 42) * mm, "end": v(34.76, 0) * mm});
            skLineSegment(sketch, "E71.4.0.1", {"start": v(34.76, 42) * mm, "end": v(33.16, 42) * mm});
            skLineSegment(sketch, "E71.4.0.2", {"start": v(33.16, 42) * mm, "end": v(33.16, 0) * mm});
            skLineSegment(sketch, "E71.4.0.3", {"start": v(34.76, 0) * mm, "end": v(33.16, 0) * mm});
            skLineSegment(sketch, "E71.5.0.0", {"start": v(70.26, 42) * mm, "end": v(70.26, 0) * mm});
            skLineSegment(sketch, "E71.5.0.1", {"start": v(70.26, 42) * mm, "end": v(68.66, 42) * mm});
            skLineSegment(sketch, "E71.5.0.2", {"start": v(68.66, 42) * mm, "end": v(68.66, 0) * mm});
            skLineSegment(sketch, "E71.5.0.3", {"start": v(70.26, 0) * mm, "end": v(68.66, 0) * mm});
            skLineSegment(sketch, "E71.6.0.0", {"start": v(105.76, 42) * mm, "end": v(105.76, 0) * mm});
            skLineSegment(sketch, "E71.6.0.1", {"start": v(105.76, 42) * mm, "end": v(104.16, 42) * mm});
            skLineSegment(sketch, "E71.6.0.2", {"start": v(104.16, 42) * mm, "end": v(104.16, 0) * mm});
            skLineSegment(sketch, "E71.6.0.3", {"start": v(105.76, 0) * mm, "end": v(104.16, 0) * mm});
            skLineSegment(sketch, "E71.7.0.0", {"start": v(141.26, 42) * mm, "end": v(141.26, 0) * mm});
            skLineSegment(sketch, "E71.7.0.1", {"start": v(141.26, 42) * mm, "end": v(139.66, 42) * mm});
            skLineSegment(sketch, "E71.7.0.2", {"start": v(139.66, 42) * mm, "end": v(139.66, 0) * mm});
            skLineSegment(sketch, "E71.7.0.3", {"start": v(141.26, 0) * mm, "end": v(139.66, 0) * mm});
            skLineSegment(sketch, "E71.direction1", {"start": v(-107.24, 0) * mm, "end": v(-71.74, 0) * mm, "construction": true});
            skSolve(sketch);
        }
        {
            var Q0;
            Q0=makeQuery(id+"F1.opExtrude","SWEPT_FACE",FACE,{"disambiguationData":[OSD([sQuery(id+"F0.wireOp",EDGE,"E9")])]});
            var sketch = newSketch(context, id + "F11", { "sketchPlane" : qUnion([Q0])});
            skPoint(sketch, "E72", {"position": v(288.38, 51.7) * mm});
            skPoint(sketch, "E73", {"position": v(256.38, 51.7) * mm});
            skPoint(sketch, "E74", {"position": v(224.38, 51.7) * mm});
            skPoint(sketch, "E75", {"position": v(192.38, 51.7) * mm});
            skPoint(sketch, "E76", {"position": v(160.38, 51.7) * mm});
            skPoint(sketch, "E77", {"position": v(128.38, 51.7) * mm});
            skLineSegment(sketch, "E78", {"start": v(288.38, 0) * mm, "end": v(288.38, 70.05) * mm, "construction": true});
            skLineSegment(sketch, "E79", {"start": v(256.38, 0) * mm, "end": v(256.38, 51.7) * mm, "construction": true});
            skLineSegment(sketch, "E80", {"start": v(224.38, 0) * mm, "end": v(224.38, 51.7) * mm, "construction": true});
            skLineSegment(sketch, "E81", {"start": v(192.38, 0) * mm, "end": v(192.38, 51.7) * mm, "construction": true});
            skLineSegment(sketch, "E82", {"start": v(160.38, 0) * mm, "end": v(160.38, 51.7) * mm, "construction": true});
            skLineSegment(sketch, "E83", {"start": v(128.38, 0) * mm, "end": v(128.38, 51.7) * mm, "construction": true});
            skLineSegment(sketch, "E84.bottom", {"start": v(289.18, 0) * mm, "end": v(287.58, 0) * mm});
            skLineSegment(sketch, "E84.top", {"start": v(289.18, 42) * mm, "end": v(287.58, 42) * mm});
            skLineSegment(sketch, "E84.left", {"start": v(289.18, 0) * mm, "end": v(289.18, 42) * mm});
            skLineSegment(sketch, "E84.right", {"start": v(287.58, 0) * mm, "end": v(287.58, 42) * mm});
            skLineSegment(sketch, "E85.bottom", {"start": v(257.18, 0) * mm, "end": v(255.57, 0) * mm});
            skLineSegment(sketch, "E85.top", {"start": v(257.18, 42) * mm, "end": v(255.57, 42) * mm});
            skLineSegment(sketch, "E85.left", {"start": v(257.18, 0) * mm, "end": v(257.18, 42) * mm});
            skLineSegment(sketch, "E85.right", {"start": v(255.57, 0) * mm, "end": v(255.57, 42) * mm});
            skLineSegment(sketch, "E86.bottom", {"start": v(225.18, 0) * mm, "end": v(223.58, 0) * mm});
            skLineSegment(sketch, "E86.top", {"start": v(225.18, 42) * mm, "end": v(223.58, 42) * mm});
            skLineSegment(sketch, "E86.left", {"start": v(225.18, 0) * mm, "end": v(225.18, 42) * mm});
            skLineSegment(sketch, "E86.right", {"start": v(223.58, 0) * mm, "end": v(223.58, 42) * mm});
            skLineSegment(sketch, "E87.bottom", {"start": v(193.18, 0) * mm, "end": v(191.58, 0) * mm});
            skLineSegment(sketch, "E87.top", {"start": v(193.18, 42) * mm, "end": v(191.58, 42) * mm});
            skLineSegment(sketch, "E87.left", {"start": v(193.18, 0) * mm, "end": v(193.18, 42) * mm});
            skLineSegment(sketch, "E87.right", {"start": v(191.58, 0) * mm, "end": v(191.58, 42) * mm});
            skLineSegment(sketch, "E88.bottom", {"start": v(161.18, 0) * mm, "end": v(159.58, 0) * mm});
            skLineSegment(sketch, "E88.top", {"start": v(161.18, 42) * mm, "end": v(159.58, 42) * mm});
            skLineSegment(sketch, "E88.left", {"start": v(161.18, 0) * mm, "end": v(161.18, 42) * mm});
            skLineSegment(sketch, "E88.right", {"start": v(159.58, 0) * mm, "end": v(159.58, 42) * mm});
            skLineSegment(sketch, "E89.bottom", {"start": v(129.18, 0) * mm, "end": v(127.58, 0) * mm});
            skLineSegment(sketch, "E89.top", {"start": v(129.18, 42) * mm, "end": v(127.58, 42) * mm});
            skLineSegment(sketch, "E89.left", {"start": v(129.18, 0) * mm, "end": v(129.18, 42) * mm});
            skLineSegment(sketch, "E89.right", {"start": v(127.58, 0) * mm, "end": v(127.58, 42) * mm});
            skLineSegment(sketch, "E90.bottom", {"start": v(102.6, 0) * mm, "end": v(103.4, 0) * mm});
            skLineSegment(sketch, "E90.top", {"start": v(102.6, 42) * mm, "end": v(103.4, 42) * mm});
            skLineSegment(sketch, "E90.left", {"start": v(102.6, 0) * mm, "end": v(102.6, 42) * mm});
            skLineSegment(sketch, "E90.right", {"start": v(103.4, 0) * mm, "end": v(103.4, 42) * mm});
            skPoint(sketch, "E91", {"position": v(326.1, 0) * mm});
            skLineSegment(sketch, "E92.bottom", {"start": v(326.1, 0) * mm, "end": v(327.7, 0) * mm});
            skLineSegment(sketch, "E92.top", {"start": v(326.1, 42) * mm, "end": v(327.7, 42) * mm});
            skLineSegment(sketch, "E92.left", {"start": v(326.1, 0) * mm, "end": v(326.1, 42) * mm});
            skLineSegment(sketch, "E92.right", {"start": v(327.7, 0) * mm, "end": v(327.7, 42) * mm});
            skSolve(sketch);
        }
        {
            var Q0;
            Q0=makeQuery(id+"F1.opExtrude","SWEPT_FACE",FACE,{"disambiguationData":[OSD([sQuery(id+"F0.wireOp",EDGE,"E8")])]});
            var sketch = newSketch(context, id + "F12", { "sketchPlane" : qUnion([Q0])});
            skLineSegment(sketch, "E93.bottom", {"start": v(-108.14, 42) * mm, "end": v(-108.94, 42) * mm});
            skLineSegment(sketch, "E93.top", {"start": v(-108.14, 0) * mm, "end": v(-108.94, 0) * mm});
            skLineSegment(sketch, "E93.left", {"start": v(-108.14, 42) * mm, "end": v(-108.14, 0) * mm});
            skLineSegment(sketch, "E93.right", {"start": v(-108.94, 42) * mm, "end": v(-108.94, 0) * mm});
            skPoint(sketch, "E94", {"position": v(-127.44, 42) * mm});
            skLineSegment(sketch, "E95.bottom", {"start": v(-127.44, 42) * mm, "end": v(-129.04, 42) * mm});
            skLineSegment(sketch, "E95.top", {"start": v(-127.44, 0) * mm, "end": v(-129.04, 0) * mm});
            skLineSegment(sketch, "E95.left", {"start": v(-127.44, 42) * mm, "end": v(-127.44, 0) * mm});
            skLineSegment(sketch, "E95.right", {"start": v(-129.04, 42) * mm, "end": v(-129.04, 0) * mm});
            skSolve(sketch);
        }
        {
            var Q0;
            Q0=makeQuery(id+"F1.opExtrude","SWEPT_FACE",FACE,{"disambiguationData":[OSD([sQuery(id+"F0.wireOp",EDGE,"E11")])]});
            var sketch = newSketch(context, id + "F13", { "sketchPlane" : qUnion([Q0])});
            skPoint(sketch, "E96", {"position": v(-11.54, 42) * mm});
            skPoint(sketch, "E97", {"position": v(89.07, 42) * mm});
            skLineSegment(sketch, "E98.bottom", {"start": v(-11.54, 42) * mm, "end": v(-13.14, 42) * mm});
            skLineSegment(sketch, "E98.top", {"start": v(-11.54, 0) * mm, "end": v(-13.14, 0) * mm});
            skLineSegment(sketch, "E98.left", {"start": v(-11.54, 42) * mm, "end": v(-11.54, 0) * mm});
            skLineSegment(sketch, "E98.right", {"start": v(-13.14, 42) * mm, "end": v(-13.14, 0) * mm});
            skLineSegment(sketch, "E99.bottom", {"start": v(89.07, 42) * mm, "end": v(90.67, 42) * mm});
            skLineSegment(sketch, "E99.top", {"start": v(89.07, 0) * mm, "end": v(90.67, 0) * mm});
            skLineSegment(sketch, "E99.left", {"start": v(89.07, 42) * mm, "end": v(89.07, 0) * mm});
            skLineSegment(sketch, "E99.right", {"start": v(90.67, 42) * mm, "end": v(90.67, 0) * mm});
            skPoint(sketch, "E100", {"position": v(38.78, 42) * mm});
            skPoint(sketch, "E101", {"position": v(38.78, 0) * mm});
            skLineSegment(sketch, "E102", {"start": v(38.78, 42) * mm, "end": v(38.78, 0) * mm, "construction": true});
            skPoint(sketch, "E103", {"position": v(22.28, 42) * mm});
            skPoint(sketch, "E104", {"position": v(55.28, 42) * mm});
            skLineSegment(sketch, "E105.bottom", {"start": v(21.48, 42) * mm, "end": v(23.08, 42) * mm});
            skLineSegment(sketch, "E105.top", {"start": v(21.48, 0) * mm, "end": v(23.08, 0) * mm});
            skLineSegment(sketch, "E105.left", {"start": v(21.48, 42) * mm, "end": v(21.48, 0) * mm});
            skLineSegment(sketch, "E105.right", {"start": v(23.08, 42) * mm, "end": v(23.08, 0) * mm});
            skLineSegment(sketch, "E106.bottom", {"start": v(54.48, 42) * mm, "end": v(56.08, 42) * mm});
            skLineSegment(sketch, "E106.top", {"start": v(54.48, 0) * mm, "end": v(56.08, 0) * mm});
            skLineSegment(sketch, "E106.left", {"start": v(54.48, 42) * mm, "end": v(54.48, 0) * mm});
            skLineSegment(sketch, "E106.right", {"start": v(56.08, 42) * mm, "end": v(56.08, 0) * mm});
            skSolve(sketch);
        }
        {
            var Q0;
            Q0=makeQuery(id+"F1.opExtrude","SWEPT_FACE",FACE,{"disambiguationData":[OSD([sQuery(id+"F0.wireOp",EDGE,"E7")])]});
            var sketch = newSketch(context, id + "F14", { "sketchPlane" : qUnion([Q0])});
            skLineSegment(sketch, "E107.bottom", {"start": v(108.14, 42) * mm, "end": v(108.94, 42) * mm});
            skLineSegment(sketch, "E107.top", {"start": v(108.14, 0) * mm, "end": v(108.94, 0) * mm});
            skLineSegment(sketch, "E107.left", {"start": v(108.14, 42) * mm, "end": v(108.14, 0) * mm});
            skLineSegment(sketch, "E107.right", {"start": v(108.94, 42) * mm, "end": v(108.94, 0) * mm});
            skPoint(sketch, "E108", {"position": v(136.98, 42) * mm});
            skLineSegment(sketch, "E109.bottom", {"start": v(136.98, 42) * mm, "end": v(138.58, 42) * mm});
            skLineSegment(sketch, "E109.top", {"start": v(136.98, 0) * mm, "end": v(138.58, 0) * mm});
            skLineSegment(sketch, "E109.left", {"start": v(136.98, 42) * mm, "end": v(136.98, 0) * mm});
            skLineSegment(sketch, "E109.right", {"start": v(138.58, 42) * mm, "end": v(138.58, 0) * mm});
            skSolve(sketch);
        }
        {
            var Q0;
            Q0=makeQuery(id+"F1.opExtrude","SWEPT_FACE",FACE,{"disambiguationData":[OSD([sQuery(id+"F0.wireOp",EDGE,"E6")])]});
            var sketch = newSketch(context, id + "F15", { "sketchPlane" : qUnion([Q0])});
            skPoint(sketch, "E110", {"position": v(-287.7, 0) * mm});
            skLineSegment(sketch, "E111.bottom", {"start": v(-287.7, 0) * mm, "end": v(-289.3, 0) * mm});
            skLineSegment(sketch, "E111.top", {"start": v(-287.7, 42) * mm, "end": v(-289.3, 42) * mm});
            skLineSegment(sketch, "E111.left", {"start": v(-287.7, 0) * mm, "end": v(-287.7, 42) * mm});
            skLineSegment(sketch, "E111.right", {"start": v(-289.3, 0) * mm, "end": v(-289.3, 42) * mm});
            skPoint(sketch, "E112", {"position": v(-288.5, 0) * mm});
            skPoint(sketch, "E113", {"position": v(-256.5, 0) * mm});
            skPoint(sketch, "E114", {"position": v(-224.5, 0) * mm});
            skPoint(sketch, "E115", {"position": v(-192.5, 0) * mm});
            skPoint(sketch, "E116", {"position": v(-160.5, 0) * mm});
            skPoint(sketch, "E117", {"position": v(-128.5, 0) * mm});
            skPoint(sketch, "E118", {"position": v(-96.5, 0) * mm});
            skPoint(sketch, "E119", {"position": v(-64.5, 0) * mm});
            skPoint(sketch, "E120", {"position": v(-32.5, 0) * mm});
            skLineSegment(sketch, "E121.bottom", {"start": v(-255.7, 0) * mm, "end": v(-257.3, 0) * mm});
            skLineSegment(sketch, "E121.top", {"start": v(-255.7, 42) * mm, "end": v(-257.3, 42) * mm});
            skLineSegment(sketch, "E121.left", {"start": v(-255.7, 0) * mm, "end": v(-255.7, 42) * mm});
            skLineSegment(sketch, "E121.right", {"start": v(-257.3, 0) * mm, "end": v(-257.3, 42) * mm});
            skLineSegment(sketch, "E122.1.0.0", {"start": v(-223.7, 0) * mm, "end": v(-223.7, 42) * mm});
            skLineSegment(sketch, "E122.1.0.1", {"start": v(-223.7, 0) * mm, "end": v(-225.3, 0) * mm});
            skLineSegment(sketch, "E122.1.0.2", {"start": v(-225.3, 0) * mm, "end": v(-225.3, 42) * mm});
            skLineSegment(sketch, "E122.1.0.3", {"start": v(-223.7, 42) * mm, "end": v(-225.3, 42) * mm});
            skLineSegment(sketch, "E122.2.0.0", {"start": v(-191.7, 0) * mm, "end": v(-191.7, 42) * mm});
            skLineSegment(sketch, "E122.2.0.1", {"start": v(-191.7, 0) * mm, "end": v(-193.3, 0) * mm});
            skLineSegment(sketch, "E122.2.0.2", {"start": v(-193.3, 0) * mm, "end": v(-193.3, 42) * mm});
            skLineSegment(sketch, "E122.2.0.3", {"start": v(-191.7, 42) * mm, "end": v(-193.3, 42) * mm});
            skLineSegment(sketch, "E122.3.0.0", {"start": v(-159.7, 0) * mm, "end": v(-159.7, 42) * mm});
            skLineSegment(sketch, "E122.3.0.1", {"start": v(-159.7, 0) * mm, "end": v(-161.3, 0) * mm});
            skLineSegment(sketch, "E122.3.0.2", {"start": v(-161.3, 0) * mm, "end": v(-161.3, 42) * mm});
            skLineSegment(sketch, "E122.3.0.3", {"start": v(-159.7, 42) * mm, "end": v(-161.3, 42) * mm});
            skLineSegment(sketch, "E122.4.0.0", {"start": v(-127.7, 0) * mm, "end": v(-127.7, 42) * mm});
            skLineSegment(sketch, "E122.4.0.1", {"start": v(-127.7, 0) * mm, "end": v(-129.3, 0) * mm});
            skLineSegment(sketch, "E122.4.0.2", {"start": v(-129.3, 0) * mm, "end": v(-129.3, 42) * mm});
            skLineSegment(sketch, "E122.4.0.3", {"start": v(-127.7, 42) * mm, "end": v(-129.3, 42) * mm});
            skLineSegment(sketch, "E122.5.0.0", {"start": v(-95.7, 0) * mm, "end": v(-95.7, 42) * mm});
            skLineSegment(sketch, "E122.5.0.1", {"start": v(-95.7, 0) * mm, "end": v(-97.3, 0) * mm});
            skLineSegment(sketch, "E122.5.0.2", {"start": v(-97.3, 0) * mm, "end": v(-97.3, 42) * mm});
            skLineSegment(sketch, "E122.5.0.3", {"start": v(-95.7, 42) * mm, "end": v(-97.3, 42) * mm});
            skLineSegment(sketch, "E122.6.0.0", {"start": v(-63.7, 0) * mm, "end": v(-63.7, 42) * mm});
            skLineSegment(sketch, "E122.6.0.1", {"start": v(-63.7, 0) * mm, "end": v(-65.3, 0) * mm});
            skLineSegment(sketch, "E122.6.0.2", {"start": v(-65.3, 0) * mm, "end": v(-65.3, 42) * mm});
            skLineSegment(sketch, "E122.6.0.3", {"start": v(-63.7, 42) * mm, "end": v(-65.3, 42) * mm});
            skLineSegment(sketch, "E122.7.0.0", {"start": v(-31.7, 0) * mm, "end": v(-31.7, 42) * mm});
            skLineSegment(sketch, "E122.7.0.1", {"start": v(-31.7, 0) * mm, "end": v(-33.3, 0) * mm});
            skLineSegment(sketch, "E122.7.0.2", {"start": v(-33.3, 0) * mm, "end": v(-33.3, 42) * mm});
            skLineSegment(sketch, "E122.7.0.3", {"start": v(-31.7, 42) * mm, "end": v(-33.3, 42) * mm});
            skLineSegment(sketch, "E122.direction1", {"start": v(-255.7, 42) * mm, "end": v(-223.7, 42) * mm, "construction": true});
            skLineSegment(sketch, "E123.bottom", {"start": v(0, 0) * mm, "end": v(-0.8, 0) * mm});
            skLineSegment(sketch, "E123.top", {"start": v(0, 42) * mm, "end": v(-0.8, 42) * mm});
            skLineSegment(sketch, "E123.left", {"start": v(0, 0) * mm, "end": v(0, 42) * mm});
            skLineSegment(sketch, "E123.right", {"start": v(-0.8, 0) * mm, "end": v(-0.8, 42) * mm});
            skSolve(sketch);
        }
        {
            var Q0;
            Q0=qSketchRegion(id+"F4",true);
            var Q1;
            Q1=qSketchRegion(id+"F6",true);
            var Q2;
            Q2=qSketchRegion(id+"F8",true);
            extrude(context, id + "F16", {"entities" : qUnion([Q0, Q1, Q2]), "operationType" : NewBodyOperationType.ADD, "depth" : .4 * mm, "offsetDistance" : 25 * mm});
        }
        {
            var Q0;
            Q0=qSketchRegion(id+"F5",true);
            var Q1;
            Q1=qSketchRegion(id+"F10",true);
            var Q2;
            Q2=qSketchRegion(id+"F12",true);
            extrude(context, id + "F17", {"entities" : qUnion([Q0, Q1, Q2]), "operationType" : NewBodyOperationType.ADD, "depth" : .4 * mm, "offsetDistance" : 25 * mm});
        }
        {
            var Q0;
            Q0=qSketchRegion(id+"F7",true);
            var Q1;
            Q1=qSketchRegion(id+"F9",true);
            var Q2;
            Q2=qSketchRegion(id+"F14",true);
            extrude(context, id + "F18", {"entities" : qUnion([Q0, Q1, Q2]), "operationType" : NewBodyOperationType.ADD, "depth" : .4 * mm, "offsetDistance" : 25 * mm});
        }
        {
            var Q0;
            Q0=qSketchRegion(id+"F11",true);
            var Q1;
            Q1=qSketchRegion(id+"F13",true);
            var Q2;
            Q2=qSketchRegion(id+"F15",true);
            extrude(context, id + "F19", {"entities" : qUnion([Q0, Q1, Q2]), "operationType" : NewBodyOperationType.ADD, "depth" : .4 * mm, "offsetDistance" : 25 * mm});
        }
        {
            var Q0;
            {var subQ9=sQuery(id+"F0.wireOp",EDGE,"E2");Q0=makeQuery(id+"F16.boolean.opBoolean","SPLIT",FACE,{"disambiguationData":[TD([makeQuery(id+"F16.opExtrude","SWEPT_FACE",FACE,{"disambiguationData":[OSD([sQuery(id+"F6.wireOp",EDGE,"E39.left")])]})])],"derivedFrom":makeQuery(id+"F1.opExtrude","SWEPT_FACE",FACE,{"disambiguationData":[OSD([subQ9])]})});}
            var sketch = newSketch(context, id + "F20", { "sketchPlane" : qUnion([Q0])});
            skLineSegment(sketch, "E124.bottom", {"start": v(-92.07, 30) * mm, "end": v(-77.93, 30) * mm});
            skLineSegment(sketch, "E124.top", {"start": v(-92.07, 12) * mm, "end": v(-77.93, 12) * mm});
            skLineSegment(sketch, "E124.left", {"start": v(-92.07, 30) * mm, "end": v(-92.07, 12) * mm});
            skLineSegment(sketch, "E124.right", {"start": v(-77.93, 30) * mm, "end": v(-77.93, 12) * mm});
            skLineSegment(sketch, "E125.0", {"start": v(-90.14, 28.07) * mm, "end": v(-85.96, 28.07) * mm});
            skLineSegment(sketch, "E125.1", {"start": v(-90.14, 28.07) * mm, "end": v(-90.14, 21.96) * mm});
            skLineSegment(sketch, "E125.2", {"start": v(-90.14, 13.93) * mm, "end": v(-85.96, 13.93) * mm});
            skLineSegment(sketch, "E125.3", {"start": v(-79.86, 28.07) * mm, "end": v(-79.86, 21.96) * mm});
            skLineSegment(sketch, "E126.left", {"start": v(-85.96, 28.07) * mm, "end": v(-85.96, 21.96) * mm});
            skLineSegment(sketch, "E126.right", {"start": v(-84.04, 28.07) * mm, "end": v(-84.04, 21.96) * mm});
            skLineSegment(sketch, "E127.bottom", {"start": v(-79.86, 21.96) * mm, "end": v(-84.04, 21.96) * mm});
            skLineSegment(sketch, "E127.top", {"start": v(-79.86, 20.04) * mm, "end": v(-84.04, 20.04) * mm});
            skLineSegment(sketch, "E128.trimOffspring", {"start": v(-85.96, 21.96) * mm, "end": v(-90.14, 21.96) * mm});
            skLineSegment(sketch, "E129.trimOffspring", {"start": v(-85.96, 20.04) * mm, "end": v(-85.96, 13.93) * mm});
            skLineSegment(sketch, "E130.trimOffspring", {"start": v(-85.96, 20.04) * mm, "end": v(-90.14, 20.04) * mm});
            skLineSegment(sketch, "E131.trimOffspring", {"start": v(-84.04, 20.04) * mm, "end": v(-84.04, 13.93) * mm});
            skLineSegment(sketch, "E132.trimOffspring", {"start": v(-79.86, 20.04) * mm, "end": v(-79.86, 13.93) * mm});
            skLineSegment(sketch, "E133.trimOffspring", {"start": v(-90.14, 20.04) * mm, "end": v(-90.14, 13.93) * mm});
            skLineSegment(sketch, "E134.trimOffspring", {"start": v(-84.04, 28.07) * mm, "end": v(-79.86, 28.07) * mm});
            skLineSegment(sketch, "E135.trimOffspring", {"start": v(-84.04, 13.93) * mm, "end": v(-79.86, 13.93) * mm});
            skSolve(sketch);
        }
        {
            var Q0;
            {var subQ9=sQuery(id+"F0.wireOp",EDGE,"E2");Q0=makeQuery(id+"F16.boolean.opBoolean","SPLIT",FACE,{"disambiguationData":[TD([makeQuery(id+"F16.opExtrude","SWEPT_FACE",FACE,{"disambiguationData":[OSD([sQuery(id+"F6.wireOp",EDGE,"E40.left")])]})])],"derivedFrom":makeQuery(id+"F1.opExtrude","SWEPT_FACE",FACE,{"disambiguationData":[OSD([subQ9])]})});}
            var sketch = newSketch(context, id + "F21", { "sketchPlane" : qUnion([Q0])});
            skLineSegment(sketch, "E136.bottom", {"start": v(-24.67, 30) * mm, "end": v(-10.53, 30) * mm});
            skLineSegment(sketch, "E136.top", {"start": v(-24.67, 12) * mm, "end": v(-10.53, 12) * mm});
            skLineSegment(sketch, "E136.left", {"start": v(-24.67, 30) * mm, "end": v(-24.67, 12) * mm});
            skLineSegment(sketch, "E136.right", {"start": v(-10.53, 30) * mm, "end": v(-10.53, 12) * mm});
            skLineSegment(sketch, "E137.0", {"start": v(-22.74, 28.07) * mm, "end": v(-18.56, 28.07) * mm});
            skLineSegment(sketch, "E137.1", {"start": v(-22.74, 28.07) * mm, "end": v(-22.74, 21.96) * mm});
            skLineSegment(sketch, "E137.2", {"start": v(-22.74, 13.93) * mm, "end": v(-18.56, 13.93) * mm});
            skLineSegment(sketch, "E137.3", {"start": v(-12.46, 28.07) * mm, "end": v(-12.46, 21.96) * mm});
            skLineSegment(sketch, "E138.left", {"start": v(-18.56, 28.07) * mm, "end": v(-18.56, 21.96) * mm});
            skLineSegment(sketch, "E138.right", {"start": v(-16.64, 28.07) * mm, "end": v(-16.64, 21.96) * mm});
            skLineSegment(sketch, "E139.bottom", {"start": v(-12.46, 21.96) * mm, "end": v(-16.64, 21.96) * mm});
            skLineSegment(sketch, "E139.top", {"start": v(-12.46, 20.04) * mm, "end": v(-16.64, 20.04) * mm});
            skLineSegment(sketch, "E140.trimOffspring", {"start": v(-18.56, 21.96) * mm, "end": v(-22.74, 21.96) * mm});
            skLineSegment(sketch, "E141.trimOffspring", {"start": v(-18.56, 20.04) * mm, "end": v(-18.56, 13.93) * mm});
            skLineSegment(sketch, "E142.trimOffspring", {"start": v(-18.56, 20.04) * mm, "end": v(-22.74, 20.04) * mm});
            skLineSegment(sketch, "E143.trimOffspring", {"start": v(-16.64, 20.04) * mm, "end": v(-16.64, 13.93) * mm});
            skLineSegment(sketch, "E144.trimOffspring", {"start": v(-12.46, 20.04) * mm, "end": v(-12.46, 13.93) * mm});
            skLineSegment(sketch, "E145.trimOffspring", {"start": v(-22.74, 20.04) * mm, "end": v(-22.74, 13.93) * mm});
            skLineSegment(sketch, "E146.trimOffspring", {"start": v(-16.64, 28.07) * mm, "end": v(-12.46, 28.07) * mm});
            skLineSegment(sketch, "E147.trimOffspring", {"start": v(-16.64, 13.93) * mm, "end": v(-12.46, 13.93) * mm});
            skSolve(sketch);
        }
        {
            var Q0;
            {var subQ11=sQuery(id+"F0.wireOp",EDGE,"E0");Q0=makeQuery(id+"F16.boolean.opBoolean","SPLIT",FACE,{"disambiguationData":[TD([makeQuery(id+"F16.opExtrude","SWEPT_FACE",FACE,{"disambiguationData":[OSD([sQuery(id+"F4.wireOp",EDGE,"E27.right")])]})])],"derivedFrom":makeQuery(id+"F1.opExtrude","SWEPT_FACE",FACE,{"disambiguationData":[OSD([subQ11])]})});}
            var sketch = newSketch(context, id + "F22", { "sketchPlane" : qUnion([Q0])});
            skLineSegment(sketch, "E148.bottom", {"start": v(-215.58, 30) * mm, "end": v(-201.43, 30) * mm});
            skLineSegment(sketch, "E148.top", {"start": v(-215.58, 12) * mm, "end": v(-201.43, 12) * mm});
            skLineSegment(sketch, "E148.left", {"start": v(-215.58, 30) * mm, "end": v(-215.58, 12) * mm});
            skLineSegment(sketch, "E148.right", {"start": v(-201.43, 30) * mm, "end": v(-201.43, 12) * mm});
            skLineSegment(sketch, "E149.0", {"start": v(-213.65, 28.07) * mm, "end": v(-209.47, 28.07) * mm});
            skLineSegment(sketch, "E149.1", {"start": v(-213.65, 28.07) * mm, "end": v(-213.65, 21.96) * mm});
            skLineSegment(sketch, "E149.2", {"start": v(-213.65, 13.93) * mm, "end": v(-209.47, 13.93) * mm});
            skLineSegment(sketch, "E149.3", {"start": v(-203.36, 28.07) * mm, "end": v(-203.36, 21.96) * mm});
            skLineSegment(sketch, "E150.left", {"start": v(-209.47, 28.07) * mm, "end": v(-209.47, 21.96) * mm});
            skLineSegment(sketch, "E150.right", {"start": v(-207.54, 28.07) * mm, "end": v(-207.54, 21.96) * mm});
            skLineSegment(sketch, "E151.bottom", {"start": v(-203.36, 21.96) * mm, "end": v(-207.54, 21.96) * mm});
            skLineSegment(sketch, "E151.top", {"start": v(-203.36, 20.04) * mm, "end": v(-207.54, 20.04) * mm});
            skLineSegment(sketch, "E152.trimOffspring", {"start": v(-209.47, 21.96) * mm, "end": v(-213.65, 21.96) * mm});
            skLineSegment(sketch, "E153.trimOffspring", {"start": v(-209.47, 20.04) * mm, "end": v(-209.47, 13.93) * mm});
            skLineSegment(sketch, "E154.trimOffspring", {"start": v(-209.47, 20.04) * mm, "end": v(-213.65, 20.04) * mm});
            skLineSegment(sketch, "E155.trimOffspring", {"start": v(-207.54, 20.04) * mm, "end": v(-207.54, 13.93) * mm});
            skLineSegment(sketch, "E156.trimOffspring", {"start": v(-203.36, 20.04) * mm, "end": v(-203.36, 13.93) * mm});
            skLineSegment(sketch, "E157.trimOffspring", {"start": v(-213.65, 20.04) * mm, "end": v(-213.65, 13.93) * mm});
            skLineSegment(sketch, "E158.trimOffspring", {"start": v(-207.54, 28.07) * mm, "end": v(-203.36, 28.07) * mm});
            skLineSegment(sketch, "E159.trimOffspring", {"start": v(-207.54, 13.93) * mm, "end": v(-203.36, 13.93) * mm});
            skSolve(sketch);
        }
        {
            var Q0;
            Q0=qSketchRegion(id+"F20",true);
            var Q1;
            Q1=qSketchRegion(id+"F21",true);
            var Q2;
            Q2=qSketchRegion(id+"F22",true);
            var Q3;
            Q3=qSketchRegion(id+"FdOBm2loh9Dp4dc_1",true);
            var Q4;
            Q4=qSketchRegion(id+"FY3zykOt8QbZdy5_1",true);
            var Q5;
            Q5=qSketchRegion(id+"FAGqtvrS7YIPi1H_1",true);
            var Q6;
            Q6=qSketchRegion(id+"FQFn3NphHTKGCZ7_1",true);
            extrude(context, id + "F23", {"entities" : qUnion([Q0, Q1, Q2, Q3, Q4, Q5, Q6]), "operationType" : NewBodyOperationType.REMOVE, "oppositeDirection" : true, "depth" : .5 * mm, "offsetDistance" : 25 * mm});
        }
        {
            var Q0;
            {var subQ11=sQuery(id+"F0.wireOp",EDGE,"E0");Q0=makeQuery(id+"F16.boolean.opBoolean","SPLIT",FACE,{"disambiguationData":[TD([makeQuery(id+"F16.opExtrude","SWEPT_FACE",FACE,{"disambiguationData":[OSD([sQuery(id+"F4.wireOp",EDGE,"E25.right")])]})])],"derivedFrom":makeQuery(id+"F1.opExtrude","SWEPT_FACE",FACE,{"disambiguationData":[OSD([subQ11])]})});}
            var sketch = newSketch(context, id + "F24", { "sketchPlane" : qUnion([Q0])});
            skLineSegment(sketch, "E160.bottom", {"start": v(-280.88, 30) * mm, "end": v(-263.88, 30) * mm});
            skLineSegment(sketch, "E160.top", {"start": v(-280.88, 0) * mm, "end": v(-263.88, 0) * mm});
            skLineSegment(sketch, "E160.left", {"start": v(-280.88, 30) * mm, "end": v(-280.88, 0) * mm});
            skLineSegment(sketch, "E160.right", {"start": v(-263.88, 30) * mm, "end": v(-263.88, 0) * mm});
            skLineSegment(sketch, "E161.0", {"start": v(-279.88, 29) * mm, "end": v(-279.88, 1) * mm});
            skLineSegment(sketch, "E161.1", {"start": v(-279.88, 29) * mm, "end": v(-264.88, 29) * mm});
            skLineSegment(sketch, "E161.2", {"start": v(-264.88, 29) * mm, "end": v(-264.88, 1) * mm});
            skLineSegment(sketch, "E161.3", {"start": v(-279.88, 1) * mm, "end": v(-264.88, 1) * mm});
            skLineSegment(sketch, "E162.0", {"start": v(-278.38, 27.5) * mm, "end": v(-278.38, 2.5) * mm});
            skLineSegment(sketch, "E162.1", {"start": v(-278.38, 27.5) * mm, "end": v(-266.38, 27.5) * mm});
            skLineSegment(sketch, "E162.2", {"start": v(-266.38, 27.5) * mm, "end": v(-266.38, 2.5) * mm});
            skLineSegment(sketch, "E162.3", {"start": v(-278.38, 2.5) * mm, "end": v(-266.38, 2.5) * mm});
            skPoint(sketch, "E163", {"position": v(-272.38, 0) * mm});
            skSolve(sketch);
        }
        {
            var Q0;
            Q0=makeQuery(id+"F24.imprint","IMPRINT",FACE,{"disambiguationData":[TD([[makeQuery(id+"F24.imprint","IMPRINT",EDGE,{"derivedFrom":sQuery(id+"F24.wireOp",EDGE,"E160.bottom")}),-1.0]])]});
            var Q1;
            Q1=makeQuery(id+"F24.imprint","IMPRINT",FACE,{"disambiguationData":[TD([[makeQuery(id+"F24.imprint","IMPRINT",EDGE,{"derivedFrom":sQuery(id+"F24.wireOp",EDGE,"E162.0")}),1.0]])]});
            extrude(context, id + "F25", {"entities" : qUnion([Q0, Q1]), "operationType" : NewBodyOperationType.REMOVE, "oppositeDirection" : true, "depth" : .5 * mm, "offsetDistance" : 25 * mm});
        }
        {
            var Q0;
            {var subQ7=sQuery(id+"F0.wireOp",EDGE,"E4");Q0=makeQuery(id+"F16.boolean.opBoolean","SPLIT",FACE,{"disambiguationData":[TD([makeQuery(id+"F16.opExtrude","SWEPT_FACE",FACE,{"disambiguationData":[OSD([sQuery(id+"F8.wireOp",EDGE,"E62.left")])]})])],"derivedFrom":makeQuery(id+"F1.opExtrude","SWEPT_FACE",FACE,{"disambiguationData":[OSD([subQ7])]})});}
            var sketch = newSketch(context, id + "F26", { "sketchPlane" : qUnion([Q0])});
            skLineSegment(sketch, "E164.bottom", {"start": v(232, 30) * mm, "end": v(249, 30) * mm});
            skLineSegment(sketch, "E164.top", {"start": v(232, 0) * mm, "end": v(249, 0) * mm});
            skLineSegment(sketch, "E164.left", {"start": v(232, 30) * mm, "end": v(232, 0) * mm});
            skLineSegment(sketch, "E164.right", {"start": v(249, 30) * mm, "end": v(249, 0) * mm});
            skLineSegment(sketch, "E165.0", {"start": v(233, 29) * mm, "end": v(233, 1) * mm});
            skLineSegment(sketch, "E165.1", {"start": v(233, 29) * mm, "end": v(248, 29) * mm});
            skLineSegment(sketch, "E165.2", {"start": v(248, 29) * mm, "end": v(248, 1) * mm});
            skLineSegment(sketch, "E165.3", {"start": v(233, 1) * mm, "end": v(248, 1) * mm});
            skLineSegment(sketch, "E166.0", {"start": v(234.5, 27.5) * mm, "end": v(234.5, 2.5) * mm});
            skLineSegment(sketch, "E166.1", {"start": v(234.5, 27.5) * mm, "end": v(246.5, 27.5) * mm});
            skLineSegment(sketch, "E166.2", {"start": v(246.5, 27.5) * mm, "end": v(246.5, 2.5) * mm});
            skLineSegment(sketch, "E166.3", {"start": v(234.5, 2.5) * mm, "end": v(246.5, 2.5) * mm});
            skPoint(sketch, "E167", {"position": v(240.5, 0) * mm});
            skSolve(sketch);
        }
        {
            var Q0;
            Q0=makeQuery(id+"F26.imprint","IMPRINT",FACE,{"disambiguationData":[TD([[makeQuery(id+"F26.imprint","IMPRINT",EDGE,{"derivedFrom":sQuery(id+"F26.wireOp",EDGE,"E164.bottom")}),-1.0]])]});
            var Q1;
            Q1=makeQuery(id+"F26.imprint","IMPRINT",FACE,{"disambiguationData":[TD([[makeQuery(id+"F26.imprint","IMPRINT",EDGE,{"derivedFrom":sQuery(id+"F26.wireOp",EDGE,"E166.0")}),1.0]])]});
            extrude(context, id + "F27", {"entities" : qUnion([Q0, Q1]), "operationType" : NewBodyOperationType.REMOVE, "oppositeDirection" : true, "depth" : .5 * mm, "offsetDistance" : 25 * mm});
        }
        {
            var Q0;
            {var subQ9=sQuery(id+"F0.wireOp",EDGE,"E2");Q0=makeQuery(id+"F16.boolean.opBoolean","SPLIT",FACE,{"disambiguationData":[TD([makeQuery(id+"F16.opExtrude","SWEPT_FACE",FACE,{"disambiguationData":[OSD([sQuery(id+"F6.wireOp",EDGE,"E46.left")])]})])],"derivedFrom":makeQuery(id+"F1.opExtrude","SWEPT_FACE",FACE,{"disambiguationData":[OSD([subQ9])]})});}
            var sketch = newSketch(context, id + "F28", { "sketchPlane" : qUnion([Q0])});
            skLineSegment(sketch, "E168.bottom", {"start": v(-67, 31) * mm, "end": v(-35.6, 31) * mm});
            skLineSegment(sketch, "E168.top", {"start": v(-67, 0) * mm, "end": v(-35.6, 0) * mm});
            skLineSegment(sketch, "E168.left", {"start": v(-67, 31) * mm, "end": v(-67, 0) * mm});
            skLineSegment(sketch, "E168.right", {"start": v(-35.6, 31) * mm, "end": v(-35.6, 0) * mm});
            skLineSegment(sketch, "E169.0", {"start": v(-65, 29) * mm, "end": v(-37.6, 29) * mm});
            skLineSegment(sketch, "E169.1", {"start": v(-65, 29) * mm, "end": v(-65, 2) * mm});
            skLineSegment(sketch, "E169.2", {"start": v(-65, 2) * mm, "end": v(-37.6, 2) * mm});
            skLineSegment(sketch, "E169.3", {"start": v(-37.6, 29) * mm, "end": v(-37.6, 2) * mm});
            skLineSegment(sketch, "E170.bottom", {"start": v(-63.39, 27) * mm, "end": v(-53.39, 27) * mm});
            skLineSegment(sketch, "E170.top", {"start": v(-63.39, 4) * mm, "end": v(-53.39, 4) * mm});
            skLineSegment(sketch, "E170.left", {"start": v(-63.39, 27) * mm, "end": v(-63.39, 4) * mm});
            skLineSegment(sketch, "E170.right", {"start": v(-53.39, 27) * mm, "end": v(-53.39, 4) * mm});
            skLineSegment(sketch, "E171.bottom", {"start": v(-49.39, 27) * mm, "end": v(-39.39, 27) * mm});
            skLineSegment(sketch, "E171.top", {"start": v(-49.39, 4) * mm, "end": v(-39.39, 4) * mm});
            skLineSegment(sketch, "E171.left", {"start": v(-49.39, 27) * mm, "end": v(-49.39, 4) * mm});
            skLineSegment(sketch, "E171.right", {"start": v(-39.39, 27) * mm, "end": v(-39.39, 4) * mm});
            skSolve(sketch);
        }
        {
            var Q0;
            Q0=makeQuery(id+"F28.imprint","IMPRINT",FACE,{"disambiguationData":[TD([[makeQuery(id+"F28.imprint","IMPRINT",EDGE,{"derivedFrom":sQuery(id+"F28.wireOp",EDGE,"E168.bottom")}),-1.0]])]});
            var Q1;
            Q1=makeQuery(id+"F28.imprint","IMPRINT",FACE,{"disambiguationData":[TD([[makeQuery(id+"F28.imprint","IMPRINT",EDGE,{"derivedFrom":sQuery(id+"F28.wireOp",EDGE,"E170.bottom")}),-1.0]])]});
            var Q2;
            Q2=makeQuery(id+"F28.imprint","IMPRINT",FACE,{"disambiguationData":[TD([[makeQuery(id+"F28.imprint","IMPRINT",EDGE,{"derivedFrom":sQuery(id+"F28.wireOp",EDGE,"E171.bottom")}),-1.0]])]});
            extrude(context, id + "F29", {"entities" : qUnion([Q0, Q1, Q2]), "operationType" : NewBodyOperationType.REMOVE, "oppositeDirection" : true, "depth" : .5 * mm, "offsetDistance" : 25 * mm});
        }
        {
            var Q0;
            {var subQ6=sQuery(id+"F0.wireOp",EDGE,"E5");Q0=makeQuery(id+"F18.boolean.opBoolean","SPLIT",FACE,{"disambiguationData":[TD([makeQuery(id+"F18.opExtrude","SWEPT_FACE",FACE,{"disambiguationData":[OSD([sQuery(id+"F9.wireOp",EDGE,"E67.1.0.0")])]})])],"derivedFrom":makeQuery(id+"F1.opExtrude","SWEPT_FACE",FACE,{"disambiguationData":[OSD([subQ6])]})});}
            var sketch = newSketch(context, id + "F30", { "sketchPlane" : qUnion([Q0])});
            skLineSegment(sketch, "E172.bottom", {"start": v(-101.41, 30) * mm, "end": v(-87.27, 30) * mm});
            skLineSegment(sketch, "E172.top", {"start": v(-101.41, 12) * mm, "end": v(-87.27, 12) * mm});
            skLineSegment(sketch, "E172.left", {"start": v(-101.41, 30) * mm, "end": v(-101.41, 12) * mm});
            skLineSegment(sketch, "E172.right", {"start": v(-87.27, 30) * mm, "end": v(-87.27, 12) * mm});
            skLineSegment(sketch, "E173.0", {"start": v(-99.49, 28.07) * mm, "end": v(-95.3, 28.07) * mm});
            skLineSegment(sketch, "E173.1", {"start": v(-99.49, 28.07) * mm, "end": v(-99.49, 21.96) * mm});
            skLineSegment(sketch, "E173.2", {"start": v(-99.49, 13.93) * mm, "end": v(-95.3, 13.93) * mm});
            skLineSegment(sketch, "E173.3", {"start": v(-89.2, 28.07) * mm, "end": v(-89.2, 21.96) * mm});
            skLineSegment(sketch, "E174.left", {"start": v(-95.3, 28.07) * mm, "end": v(-95.3, 21.96) * mm});
            skLineSegment(sketch, "E174.right", {"start": v(-93.38, 28.07) * mm, "end": v(-93.38, 21.96) * mm});
            skLineSegment(sketch, "E175.bottom", {"start": v(-89.2, 21.96) * mm, "end": v(-93.38, 21.96) * mm});
            skLineSegment(sketch, "E175.top", {"start": v(-89.2, 20.04) * mm, "end": v(-93.38, 20.04) * mm});
            skLineSegment(sketch, "E176.trimOffspring", {"start": v(-95.3, 21.96) * mm, "end": v(-99.49, 21.96) * mm});
            skLineSegment(sketch, "E177.trimOffspring", {"start": v(-95.3, 20.04) * mm, "end": v(-95.3, 13.93) * mm});
            skLineSegment(sketch, "E178.trimOffspring", {"start": v(-95.3, 20.04) * mm, "end": v(-99.49, 20.04) * mm});
            skLineSegment(sketch, "E179.trimOffspring", {"start": v(-93.38, 20.04) * mm, "end": v(-93.38, 13.93) * mm});
            skLineSegment(sketch, "E180.trimOffspring", {"start": v(-89.2, 20.04) * mm, "end": v(-89.2, 13.93) * mm});
            skLineSegment(sketch, "E181.trimOffspring", {"start": v(-99.49, 20.04) * mm, "end": v(-99.49, 13.93) * mm});
            skLineSegment(sketch, "E182.trimOffspring", {"start": v(-93.38, 28.07) * mm, "end": v(-89.2, 28.07) * mm});
            skLineSegment(sketch, "E183.trimOffspring", {"start": v(-93.38, 13.93) * mm, "end": v(-89.2, 13.93) * mm});
            skLineSegment(sketch, "E184.bottom", {"start": v(-87.27, 30) * mm, "end": v(-73.13, 30) * mm});
            skLineSegment(sketch, "E184.top", {"start": v(-87.27, 12) * mm, "end": v(-73.13, 12) * mm});
            skLineSegment(sketch, "E184.right", {"start": v(-73.13, 30) * mm, "end": v(-73.13, 12) * mm});
            skLineSegment(sketch, "E185.0", {"start": v(-85.34, 28.07) * mm, "end": v(-81.16, 28.07) * mm});
            skLineSegment(sketch, "E185.1", {"start": v(-85.34, 28.07) * mm, "end": v(-85.34, 21.96) * mm});
            skLineSegment(sketch, "E185.2", {"start": v(-85.34, 13.93) * mm, "end": v(-81.16, 13.93) * mm});
            skLineSegment(sketch, "E185.3", {"start": v(-75.06, 28.07) * mm, "end": v(-75.06, 21.96) * mm});
            skLineSegment(sketch, "E186.left", {"start": v(-81.16, 28.07) * mm, "end": v(-81.16, 21.96) * mm});
            skLineSegment(sketch, "E186.right", {"start": v(-79.24, 28.07) * mm, "end": v(-79.24, 21.96) * mm});
            skLineSegment(sketch, "E187.bottom", {"start": v(-75.06, 21.96) * mm, "end": v(-79.24, 21.96) * mm});
            skLineSegment(sketch, "E187.top", {"start": v(-75.06, 20.04) * mm, "end": v(-79.24, 20.04) * mm});
            skLineSegment(sketch, "E188.trimOffspring", {"start": v(-81.16, 21.96) * mm, "end": v(-85.34, 21.96) * mm});
            skLineSegment(sketch, "E189.trimOffspring", {"start": v(-81.16, 20.04) * mm, "end": v(-81.16, 13.93) * mm});
            skLineSegment(sketch, "E190.trimOffspring", {"start": v(-81.16, 20.04) * mm, "end": v(-85.34, 20.04) * mm});
            skLineSegment(sketch, "E191.trimOffspring", {"start": v(-79.24, 20.04) * mm, "end": v(-79.24, 13.93) * mm});
            skLineSegment(sketch, "E192.trimOffspring", {"start": v(-75.06, 20.04) * mm, "end": v(-75.06, 13.93) * mm});
            skLineSegment(sketch, "E193.trimOffspring", {"start": v(-85.34, 20.04) * mm, "end": v(-85.34, 13.93) * mm});
            skLineSegment(sketch, "E194.trimOffspring", {"start": v(-79.24, 28.07) * mm, "end": v(-75.06, 28.07) * mm});
            skLineSegment(sketch, "E195.trimOffspring", {"start": v(-79.24, 13.93) * mm, "end": v(-75.06, 13.93) * mm});
            skSolve(sketch);
        }
        {
            var Q0;
            {var subQ6=sQuery(id+"F0.wireOp",EDGE,"E5");Q0=makeQuery(id+"F18.boolean.opBoolean","SPLIT",FACE,{"disambiguationData":[TD([makeQuery(id+"F18.opExtrude","SWEPT_FACE",FACE,{"disambiguationData":[OSD([sQuery(id+"F9.wireOp",EDGE,"E67.3.0.0")])]})])],"derivedFrom":makeQuery(id+"F1.opExtrude","SWEPT_FACE",FACE,{"disambiguationData":[OSD([subQ6])]})});}
            var sketch = newSketch(context, id + "F31", { "sketchPlane" : qUnion([Q0])});
            skLineSegment(sketch, "E196.bottom", {"start": v(-30.5, 30) * mm, "end": v(-16.36, 30) * mm});
            skLineSegment(sketch, "E196.top", {"start": v(-30.5, 12) * mm, "end": v(-16.36, 12) * mm});
            skLineSegment(sketch, "E196.left", {"start": v(-30.5, 30) * mm, "end": v(-30.5, 12) * mm});
            skLineSegment(sketch, "E196.right", {"start": v(-16.36, 30) * mm, "end": v(-16.36, 12) * mm});
            skLineSegment(sketch, "E197.0", {"start": v(-28.57, 28.07) * mm, "end": v(-24.4, 28.07) * mm});
            skLineSegment(sketch, "E197.1", {"start": v(-28.57, 28.07) * mm, "end": v(-28.57, 21.96) * mm});
            skLineSegment(sketch, "E197.2", {"start": v(-28.57, 13.93) * mm, "end": v(-24.4, 13.93) * mm});
            skLineSegment(sketch, "E197.3", {"start": v(-18.29, 28.07) * mm, "end": v(-18.29, 21.96) * mm});
            skLineSegment(sketch, "E198.left", {"start": v(-24.4, 28.07) * mm, "end": v(-24.4, 21.96) * mm});
            skLineSegment(sketch, "E198.right", {"start": v(-22.46, 28.07) * mm, "end": v(-22.46, 21.96) * mm});
            skLineSegment(sketch, "E199.bottom", {"start": v(-18.29, 21.96) * mm, "end": v(-22.46, 21.96) * mm});
            skLineSegment(sketch, "E199.top", {"start": v(-18.29, 20.04) * mm, "end": v(-22.46, 20.04) * mm});
            skLineSegment(sketch, "E200.trimOffspring", {"start": v(-24.4, 21.96) * mm, "end": v(-28.57, 21.96) * mm});
            skLineSegment(sketch, "E201.trimOffspring", {"start": v(-24.4, 20.04) * mm, "end": v(-24.4, 13.93) * mm});
            skLineSegment(sketch, "E202.trimOffspring", {"start": v(-24.4, 20.04) * mm, "end": v(-28.57, 20.04) * mm});
            skLineSegment(sketch, "E203.trimOffspring", {"start": v(-22.46, 20.04) * mm, "end": v(-22.46, 13.93) * mm});
            skLineSegment(sketch, "E204.trimOffspring", {"start": v(-18.29, 20.04) * mm, "end": v(-18.29, 13.93) * mm});
            skLineSegment(sketch, "E205.trimOffspring", {"start": v(-28.57, 20.04) * mm, "end": v(-28.57, 13.93) * mm});
            skLineSegment(sketch, "E206.trimOffspring", {"start": v(-22.46, 28.07) * mm, "end": v(-18.29, 28.07) * mm});
            skLineSegment(sketch, "E207.trimOffspring", {"start": v(-22.46, 13.93) * mm, "end": v(-18.29, 13.93) * mm});
            skLineSegment(sketch, "E208.bottom", {"start": v(-16.36, 30) * mm, "end": v(-2.21, 30) * mm});
            skLineSegment(sketch, "E208.top", {"start": v(-16.36, 12) * mm, "end": v(-2.21, 12) * mm});
            skLineSegment(sketch, "E208.right", {"start": v(-2.21, 30) * mm, "end": v(-2.21, 12) * mm});
            skLineSegment(sketch, "E209.0", {"start": v(-14.43, 28.07) * mm, "end": v(-10.25, 28.07) * mm});
            skLineSegment(sketch, "E209.1", {"start": v(-14.43, 28.07) * mm, "end": v(-14.43, 21.96) * mm});
            skLineSegment(sketch, "E209.2", {"start": v(-14.43, 13.93) * mm, "end": v(-10.25, 13.93) * mm});
            skLineSegment(sketch, "E209.3", {"start": v(-4.14, 28.07) * mm, "end": v(-4.14, 21.96) * mm});
            skLineSegment(sketch, "E210.left", {"start": v(-10.25, 28.07) * mm, "end": v(-10.25, 21.96) * mm});
            skLineSegment(sketch, "E210.right", {"start": v(-8.32, 28.07) * mm, "end": v(-8.32, 21.96) * mm});
            skLineSegment(sketch, "E211.bottom", {"start": v(-4.14, 21.96) * mm, "end": v(-8.32, 21.96) * mm});
            skLineSegment(sketch, "E211.top", {"start": v(-4.14, 20.04) * mm, "end": v(-8.32, 20.04) * mm});
            skLineSegment(sketch, "E212.trimOffspring", {"start": v(-10.25, 21.96) * mm, "end": v(-14.43, 21.96) * mm});
            skLineSegment(sketch, "E213.trimOffspring", {"start": v(-10.25, 20.04) * mm, "end": v(-10.25, 13.93) * mm});
            skLineSegment(sketch, "E214.trimOffspring", {"start": v(-10.25, 20.04) * mm, "end": v(-14.43, 20.04) * mm});
            skLineSegment(sketch, "E215.trimOffspring", {"start": v(-8.32, 20.04) * mm, "end": v(-8.32, 13.93) * mm});
            skLineSegment(sketch, "E216.trimOffspring", {"start": v(-4.14, 20.04) * mm, "end": v(-4.14, 13.93) * mm});
            skLineSegment(sketch, "E217.trimOffspring", {"start": v(-14.43, 20.04) * mm, "end": v(-14.43, 13.93) * mm});
            skLineSegment(sketch, "E218.trimOffspring", {"start": v(-8.32, 28.07) * mm, "end": v(-4.14, 28.07) * mm});
            skLineSegment(sketch, "E219.trimOffspring", {"start": v(-8.32, 13.93) * mm, "end": v(-4.14, 13.93) * mm});
            skSolve(sketch);
        }
        {
            var Q0;
            {var subQ6=sQuery(id+"F0.wireOp",EDGE,"E5");Q0=makeQuery(id+"F18.boolean.opBoolean","SPLIT",FACE,{"disambiguationData":[TD([makeQuery(id+"F18.opExtrude","SWEPT_FACE",FACE,{"disambiguationData":[OSD([sQuery(id+"F9.wireOp",EDGE,"E67.5.0.0")])]})])],"derivedFrom":makeQuery(id+"F1.opExtrude","SWEPT_FACE",FACE,{"disambiguationData":[OSD([subQ6])]})});}
            var sketch = newSketch(context, id + "F32", { "sketchPlane" : qUnion([Q0])});
            skLineSegment(sketch, "E220.bottom", {"start": v(40.41, 30) * mm, "end": v(54.56, 30) * mm});
            skLineSegment(sketch, "E220.top", {"start": v(40.41, 12) * mm, "end": v(54.56, 12) * mm});
            skLineSegment(sketch, "E220.left", {"start": v(40.41, 30) * mm, "end": v(40.41, 12) * mm});
            skLineSegment(sketch, "E220.right", {"start": v(54.56, 30) * mm, "end": v(54.56, 12) * mm});
            skLineSegment(sketch, "E221.0", {"start": v(42.34, 28.07) * mm, "end": v(46.52, 28.07) * mm});
            skLineSegment(sketch, "E221.1", {"start": v(42.34, 28.07) * mm, "end": v(42.34, 21.96) * mm});
            skLineSegment(sketch, "E221.2", {"start": v(42.34, 13.93) * mm, "end": v(46.52, 13.93) * mm});
            skLineSegment(sketch, "E221.3", {"start": v(52.63, 28.07) * mm, "end": v(52.63, 21.96) * mm});
            skLineSegment(sketch, "E222.left", {"start": v(46.52, 28.07) * mm, "end": v(46.52, 21.96) * mm});
            skLineSegment(sketch, "E222.right", {"start": v(48.45, 28.07) * mm, "end": v(48.45, 21.96) * mm});
            skLineSegment(sketch, "E223.bottom", {"start": v(52.63, 21.96) * mm, "end": v(48.45, 21.96) * mm});
            skLineSegment(sketch, "E223.top", {"start": v(52.63, 20.04) * mm, "end": v(48.45, 20.04) * mm});
            skLineSegment(sketch, "E224.trimOffspring", {"start": v(46.52, 21.96) * mm, "end": v(42.34, 21.96) * mm});
            skLineSegment(sketch, "E225.trimOffspring", {"start": v(46.52, 20.04) * mm, "end": v(46.52, 13.93) * mm});
            skLineSegment(sketch, "E226.trimOffspring", {"start": v(46.52, 20.04) * mm, "end": v(42.34, 20.04) * mm});
            skLineSegment(sketch, "E227.trimOffspring", {"start": v(48.45, 20.04) * mm, "end": v(48.45, 13.93) * mm});
            skLineSegment(sketch, "E228.trimOffspring", {"start": v(52.63, 20.04) * mm, "end": v(52.63, 13.93) * mm});
            skLineSegment(sketch, "E229.trimOffspring", {"start": v(42.34, 20.04) * mm, "end": v(42.34, 13.93) * mm});
            skLineSegment(sketch, "E230.trimOffspring", {"start": v(48.45, 28.07) * mm, "end": v(52.63, 28.07) * mm});
            skLineSegment(sketch, "E231.trimOffspring", {"start": v(48.45, 13.93) * mm, "end": v(52.63, 13.93) * mm});
            skLineSegment(sketch, "E232.bottom", {"start": v(54.56, 30) * mm, "end": v(68.7, 30) * mm});
            skLineSegment(sketch, "E232.top", {"start": v(54.56, 12) * mm, "end": v(68.7, 12) * mm});
            skLineSegment(sketch, "E232.right", {"start": v(68.7, 30) * mm, "end": v(68.7, 12) * mm});
            skLineSegment(sketch, "E233.0", {"start": v(56.49, 28.07) * mm, "end": v(60.66, 28.07) * mm});
            skLineSegment(sketch, "E233.1", {"start": v(56.49, 28.07) * mm, "end": v(56.49, 21.96) * mm});
            skLineSegment(sketch, "E233.2", {"start": v(56.49, 13.93) * mm, "end": v(60.66, 13.93) * mm});
            skLineSegment(sketch, "E233.3", {"start": v(66.77, 28.07) * mm, "end": v(66.77, 21.96) * mm});
            skLineSegment(sketch, "E234.left", {"start": v(60.66, 28.07) * mm, "end": v(60.66, 21.96) * mm});
            skLineSegment(sketch, "E234.right", {"start": v(62.6, 28.07) * mm, "end": v(62.6, 21.96) * mm});
            skLineSegment(sketch, "E235.bottom", {"start": v(66.77, 21.96) * mm, "end": v(62.6, 21.96) * mm});
            skLineSegment(sketch, "E235.top", {"start": v(66.77, 20.04) * mm, "end": v(62.6, 20.04) * mm});
            skLineSegment(sketch, "E236.trimOffspring", {"start": v(60.66, 21.96) * mm, "end": v(56.49, 21.96) * mm});
            skLineSegment(sketch, "E237.trimOffspring", {"start": v(60.66, 20.04) * mm, "end": v(60.66, 13.93) * mm});
            skLineSegment(sketch, "E238.trimOffspring", {"start": v(60.66, 20.04) * mm, "end": v(56.49, 20.04) * mm});
            skLineSegment(sketch, "E239.trimOffspring", {"start": v(62.6, 20.04) * mm, "end": v(62.6, 13.93) * mm});
            skLineSegment(sketch, "E240.trimOffspring", {"start": v(66.77, 20.04) * mm, "end": v(66.77, 13.93) * mm});
            skLineSegment(sketch, "E241.trimOffspring", {"start": v(56.49, 20.04) * mm, "end": v(56.49, 13.93) * mm});
            skLineSegment(sketch, "E242.trimOffspring", {"start": v(62.6, 28.07) * mm, "end": v(66.77, 28.07) * mm});
            skLineSegment(sketch, "E243.trimOffspring", {"start": v(62.6, 13.93) * mm, "end": v(66.77, 13.93) * mm});
            skSolve(sketch);
        }
        {
            var Q0;
            Q0=qSketchRegion(id+"F32",true);
            var Q1;
            Q1=qSketchRegion(id+"F31",true);
            var Q2;
            Q2=qSketchRegion(id+"F30",true);
            extrude(context, id + "F33", {"entities" : qUnion([Q0, Q1, Q2]), "operationType" : NewBodyOperationType.REMOVE, "oppositeDirection" : true, "depth" : .5 * mm, "offsetDistance" : 25 * mm});
        }
        {
            var Q0;
            Q0=makeQuery(id+"F1.opExtrude","SWEPT_FACE",FACE,{"disambiguationData":[OSD([sQuery(id+"F0.wireOp",EDGE,"E7")])]});
            var sketch = newSketch(context, id + "F34", { "sketchPlane" : qUnion([Q0])});
            skLineSegment(sketch, "E244.bottom", {"start": v(114.46, 30) * mm, "end": v(131.46, 30) * mm});
            skLineSegment(sketch, "E244.top", {"start": v(114.46, 0) * mm, "end": v(131.46, 0) * mm});
            skLineSegment(sketch, "E244.left", {"start": v(114.46, 30) * mm, "end": v(114.46, 0) * mm});
            skLineSegment(sketch, "E244.right", {"start": v(131.46, 30) * mm, "end": v(131.46, 0) * mm});
            skLineSegment(sketch, "E245.0", {"start": v(115.46, 29) * mm, "end": v(115.46, 1) * mm});
            skLineSegment(sketch, "E245.1", {"start": v(115.46, 29) * mm, "end": v(130.46, 29) * mm});
            skLineSegment(sketch, "E245.2", {"start": v(130.46, 29) * mm, "end": v(130.46, 1) * mm});
            skLineSegment(sketch, "E245.3", {"start": v(115.46, 1) * mm, "end": v(130.46, 1) * mm});
            skLineSegment(sketch, "E246.0", {"start": v(116.96, 27.5) * mm, "end": v(116.96, 2.5) * mm});
            skLineSegment(sketch, "E246.1", {"start": v(116.96, 27.5) * mm, "end": v(128.96, 27.5) * mm});
            skLineSegment(sketch, "E246.2", {"start": v(128.96, 27.5) * mm, "end": v(128.96, 2.5) * mm});
            skLineSegment(sketch, "E246.3", {"start": v(116.96, 2.5) * mm, "end": v(128.96, 2.5) * mm});
            skPoint(sketch, "E247", {"position": v(122.96, 0) * mm});
            skSolve(sketch);
        }
        {
            var Q0;
            Q0=qSketchRegion(id+"F34",true);
            var Q1;
            Q1=makeQuery(id+"F34.imprint","IMPRINT",FACE,{"disambiguationData":[TD([[makeQuery(id+"F34.imprint","IMPRINT",EDGE,{"derivedFrom":sQuery(id+"F34.wireOp",EDGE,"E246.0")}),1.0]])]});
            extrude(context, id + "F35", {"entities" : qUnion([Q0, Q1]), "operationType" : NewBodyOperationType.REMOVE, "oppositeDirection" : true, "depth" : .5 * mm, "offsetDistance" : 25 * mm});
        }
        {
            var Q0;
            {var subQ0=sQuery(id+"F0.wireOp",EDGE,"E11");Q0=makeQuery(id+"F19.boolean.opBoolean","SPLIT",FACE,{"disambiguationData":[TD([makeQuery(id+"F19.opExtrude","SWEPT_FACE",FACE,{"disambiguationData":[OSD([sQuery(id+"F13.wireOp",EDGE,"E105.right")])]})])],"derivedFrom":makeQuery(id+"F1.opExtrude","SWEPT_FACE",FACE,{"disambiguationData":[OSD([subQ0])]})});}
            var sketch = newSketch(context, id + "F36", { "sketchPlane" : qUnion([Q0])});
            skLineSegment(sketch, "E248.bottom", {"start": v(30.97, 30) * mm, "end": v(45.12, 30) * mm});
            skLineSegment(sketch, "E248.top", {"start": v(30.97, 12) * mm, "end": v(45.12, 12) * mm});
            skLineSegment(sketch, "E248.left", {"start": v(30.97, 30) * mm, "end": v(30.97, 12) * mm});
            skLineSegment(sketch, "E248.right", {"start": v(45.12, 30) * mm, "end": v(45.12, 12) * mm});
            skLineSegment(sketch, "E249.0", {"start": v(32.9, 28.07) * mm, "end": v(37.08, 28.07) * mm});
            skLineSegment(sketch, "E249.1", {"start": v(32.9, 28.07) * mm, "end": v(32.9, 21.96) * mm});
            skLineSegment(sketch, "E249.2", {"start": v(32.9, 13.93) * mm, "end": v(37.08, 13.93) * mm});
            skLineSegment(sketch, "E249.3", {"start": v(43.19, 28.07) * mm, "end": v(43.19, 21.96) * mm});
            skLineSegment(sketch, "E250.left", {"start": v(37.08, 28.07) * mm, "end": v(37.08, 21.96) * mm});
            skLineSegment(sketch, "E250.right", {"start": v(39.01, 28.07) * mm, "end": v(39.01, 21.96) * mm});
            skLineSegment(sketch, "E251.bottom", {"start": v(43.19, 21.96) * mm, "end": v(39.01, 21.96) * mm});
            skLineSegment(sketch, "E251.top", {"start": v(43.19, 20.04) * mm, "end": v(39.01, 20.04) * mm});
            skLineSegment(sketch, "E252.trimOffspring", {"start": v(37.08, 21.96) * mm, "end": v(32.9, 21.96) * mm});
            skLineSegment(sketch, "E253.trimOffspring", {"start": v(37.08, 20.04) * mm, "end": v(37.08, 13.93) * mm});
            skLineSegment(sketch, "E254.trimOffspring", {"start": v(37.08, 20.04) * mm, "end": v(32.9, 20.04) * mm});
            skLineSegment(sketch, "E255.trimOffspring", {"start": v(39.01, 20.04) * mm, "end": v(39.01, 13.93) * mm});
            skLineSegment(sketch, "E256.trimOffspring", {"start": v(43.19, 20.04) * mm, "end": v(43.19, 13.93) * mm});
            skLineSegment(sketch, "E257.trimOffspring", {"start": v(32.9, 20.04) * mm, "end": v(32.9, 13.93) * mm});
            skLineSegment(sketch, "E258.trimOffspring", {"start": v(39.01, 28.07) * mm, "end": v(43.19, 28.07) * mm});
            skLineSegment(sketch, "E259.trimOffspring", {"start": v(39.01, 13.93) * mm, "end": v(43.19, 13.93) * mm});
            skLineSegment(sketch, "E260.bottom", {"start": v(-2.03, 30) * mm, "end": v(12.12, 30) * mm});
            skLineSegment(sketch, "E260.top", {"start": v(-2.03, 12) * mm, "end": v(12.12, 12) * mm});
            skLineSegment(sketch, "E260.left", {"start": v(-2.03, 30) * mm, "end": v(-2.03, 12) * mm});
            skLineSegment(sketch, "E260.right", {"start": v(12.12, 30) * mm, "end": v(12.12, 12) * mm});
            skLineSegment(sketch, "E261.0", {"start": v(-0.1, 28.07) * mm, "end": v(4.08, 28.07) * mm});
            skLineSegment(sketch, "E261.1", {"start": v(-0.1, 28.07) * mm, "end": v(-0.1, 21.96) * mm});
            skLineSegment(sketch, "E261.2", {"start": v(-0.1, 13.93) * mm, "end": v(4.08, 13.93) * mm});
            skLineSegment(sketch, "E261.3", {"start": v(10.19, 28.07) * mm, "end": v(10.19, 21.96) * mm});
            skLineSegment(sketch, "E262.left", {"start": v(4.08, 28.07) * mm, "end": v(4.08, 21.96) * mm});
            skLineSegment(sketch, "E262.right", {"start": v(6.01, 28.07) * mm, "end": v(6.01, 21.96) * mm});
            skLineSegment(sketch, "E263.bottom", {"start": v(10.19, 21.96) * mm, "end": v(6.01, 21.96) * mm});
            skLineSegment(sketch, "E263.top", {"start": v(10.19, 20.04) * mm, "end": v(6.01, 20.04) * mm});
            skLineSegment(sketch, "E264.trimOffspring", {"start": v(4.08, 21.96) * mm, "end": v(-0.1, 21.96) * mm});
            skLineSegment(sketch, "E265.trimOffspring", {"start": v(4.08, 20.04) * mm, "end": v(4.08, 13.93) * mm});
            skLineSegment(sketch, "E266.trimOffspring", {"start": v(4.08, 20.04) * mm, "end": v(-0.1, 20.04) * mm});
            skLineSegment(sketch, "E267.trimOffspring", {"start": v(6.01, 20.04) * mm, "end": v(6.01, 13.93) * mm});
            skLineSegment(sketch, "E268.trimOffspring", {"start": v(10.19, 20.04) * mm, "end": v(10.19, 13.93) * mm});
            skLineSegment(sketch, "E269.trimOffspring", {"start": v(-0.1, 20.04) * mm, "end": v(-0.1, 13.93) * mm});
            skLineSegment(sketch, "E270.trimOffspring", {"start": v(6.01, 28.07) * mm, "end": v(10.19, 28.07) * mm});
            skLineSegment(sketch, "E271.trimOffspring", {"start": v(6.01, 13.93) * mm, "end": v(10.19, 13.93) * mm});
            skLineSegment(sketch, "E272.bottom", {"start": v(65.37, 30) * mm, "end": v(79.52, 30) * mm});
            skLineSegment(sketch, "E272.top", {"start": v(65.37, 12) * mm, "end": v(79.52, 12) * mm});
            skLineSegment(sketch, "E272.left", {"start": v(65.37, 30) * mm, "end": v(65.37, 12) * mm});
            skLineSegment(sketch, "E272.right", {"start": v(79.52, 30) * mm, "end": v(79.52, 12) * mm});
            skLineSegment(sketch, "E273.0", {"start": v(67.3, 28.07) * mm, "end": v(71.48, 28.07) * mm});
            skLineSegment(sketch, "E273.1", {"start": v(67.3, 28.07) * mm, "end": v(67.3, 21.96) * mm});
            skLineSegment(sketch, "E273.2", {"start": v(67.3, 13.93) * mm, "end": v(71.48, 13.93) * mm});
            skLineSegment(sketch, "E273.3", {"start": v(77.59, 28.07) * mm, "end": v(77.59, 21.96) * mm});
            skLineSegment(sketch, "E274.left", {"start": v(71.48, 28.07) * mm, "end": v(71.48, 21.96) * mm});
            skLineSegment(sketch, "E274.right", {"start": v(73.41, 28.07) * mm, "end": v(73.41, 21.96) * mm});
            skLineSegment(sketch, "E275.bottom", {"start": v(77.59, 21.96) * mm, "end": v(73.41, 21.96) * mm});
            skLineSegment(sketch, "E275.top", {"start": v(77.59, 20.04) * mm, "end": v(73.41, 20.04) * mm});
            skLineSegment(sketch, "E276.trimOffspring", {"start": v(71.48, 21.96) * mm, "end": v(67.3, 21.96) * mm});
            skLineSegment(sketch, "E277.trimOffspring", {"start": v(71.48, 20.04) * mm, "end": v(71.48, 13.93) * mm});
            skLineSegment(sketch, "E278.trimOffspring", {"start": v(71.48, 20.04) * mm, "end": v(67.3, 20.04) * mm});
            skLineSegment(sketch, "E279.trimOffspring", {"start": v(73.41, 20.04) * mm, "end": v(73.41, 13.93) * mm});
            skLineSegment(sketch, "E280.trimOffspring", {"start": v(77.59, 20.04) * mm, "end": v(77.59, 13.93) * mm});
            skLineSegment(sketch, "E281.trimOffspring", {"start": v(67.3, 20.04) * mm, "end": v(67.3, 13.93) * mm});
            skLineSegment(sketch, "E282.trimOffspring", {"start": v(73.41, 28.07) * mm, "end": v(77.59, 28.07) * mm});
            skLineSegment(sketch, "E283.trimOffspring", {"start": v(73.41, 13.93) * mm, "end": v(77.59, 13.93) * mm});
            skSolve(sketch);
        }
        {
            var Q0;
            {var subQ2=sQuery(id+"F0.wireOp",EDGE,"E9");Q0=makeQuery(id+"F19.boolean.opBoolean","SPLIT",FACE,{"disambiguationData":[TD([makeQuery(id+"F19.opExtrude","SWEPT_FACE",FACE,{"disambiguationData":[OSD([sQuery(id+"F11.wireOp",EDGE,"E84.right")])]})])],"derivedFrom":makeQuery(id+"F1.opExtrude","SWEPT_FACE",FACE,{"disambiguationData":[OSD([subQ2])]})});}
            var sketch = newSketch(context, id + "F37", { "sketchPlane" : qUnion([Q0])});
            skLineSegment(sketch, "E284.bottom", {"start": v(257.18, 31) * mm, "end": v(287.58, 31) * mm});
            skLineSegment(sketch, "E284.top", {"start": v(257.18, 0) * mm, "end": v(287.58, 0) * mm});
            skLineSegment(sketch, "E284.left", {"start": v(257.18, 31) * mm, "end": v(257.18, 0) * mm});
            skLineSegment(sketch, "E284.right", {"start": v(287.58, 31) * mm, "end": v(287.58, 0) * mm});
            skLineSegment(sketch, "E285.0", {"start": v(259.18, 29) * mm, "end": v(285.58, 29) * mm});
            skLineSegment(sketch, "E285.1", {"start": v(259.18, 29) * mm, "end": v(259.18, 2) * mm});
            skLineSegment(sketch, "E285.2", {"start": v(259.18, 2) * mm, "end": v(285.58, 2) * mm});
            skLineSegment(sketch, "E285.3", {"start": v(285.58, 29) * mm, "end": v(285.58, 2) * mm});
            skLineSegment(sketch, "E286.bottom", {"start": v(260.79, 27) * mm, "end": v(270.79, 27) * mm});
            skLineSegment(sketch, "E286.top", {"start": v(260.79, 4) * mm, "end": v(270.79, 4) * mm});
            skLineSegment(sketch, "E286.left", {"start": v(260.79, 27) * mm, "end": v(260.79, 4) * mm});
            skLineSegment(sketch, "E286.right", {"start": v(270.79, 27) * mm, "end": v(270.79, 4) * mm});
            skLineSegment(sketch, "E287.bottom", {"start": v(274.79, 27) * mm, "end": v(284.79, 27) * mm});
            skLineSegment(sketch, "E287.top", {"start": v(274.79, 4) * mm, "end": v(284.79, 4) * mm});
            skLineSegment(sketch, "E287.left", {"start": v(274.79, 27) * mm, "end": v(274.79, 4) * mm});
            skLineSegment(sketch, "E287.right", {"start": v(284.79, 27) * mm, "end": v(284.79, 4) * mm});
            skPoint(sketch, "E288", {"position": v(272.38, 0) * mm});
            skSolve(sketch);
        }
        {
            var Q0;
            Q0=qSketchRegion(id+"FRCOmFyM6VvSc9A_1",true);
            var Q1;
            Q1=qSketchRegion(id+"F36",true);
            var Q2;
            Q2=qSketchRegion(id+"F37",true);
            var Q3;
            Q3=makeQuery(id+"F37.imprint","IMPRINT",FACE,{"disambiguationData":[TD([[makeQuery(id+"F37.imprint","IMPRINT",EDGE,{"derivedFrom":sQuery(id+"F37.wireOp",EDGE,"E286.bottom")}),-1.0]])]});
            var Q4;
            Q4=makeQuery(id+"F37.imprint","IMPRINT",FACE,{"disambiguationData":[TD([[makeQuery(id+"F37.imprint","IMPRINT",EDGE,{"derivedFrom":sQuery(id+"F37.wireOp",EDGE,"E287.bottom")}),-1.0]])]});
            extrude(context, id + "F38", {"entities" : qUnion([Q0, Q1, Q2, Q3, Q4]), "operationType" : NewBodyOperationType.REMOVE, "oppositeDirection" : true, "depth" : .5 * mm, "offsetDistance" : 25 * mm});
        }
        {
            var Q0;
            {var subQ11=sQuery(id+"F0.wireOp",EDGE,"E0");Q0=makeQuery(id+"F16.boolean.opBoolean","SPLIT",FACE,{"disambiguationData":[TD([makeQuery(id+"F16.opExtrude","SWEPT_FACE",FACE,{"disambiguationData":[OSD([sQuery(id+"F4.wireOp",EDGE,"E26.right")])]})])],"derivedFrom":makeQuery(id+"F1.opExtrude","SWEPT_FACE",FACE,{"disambiguationData":[OSD([subQ11])]})});}
            var sketch = newSketch(context, id + "F39", { "sketchPlane" : qUnion([Q0])});
            skLineSegment(sketch, "E289.bottom", {"start": v(-247.57, 30) * mm, "end": v(-233.43, 30) * mm});
            skLineSegment(sketch, "E289.top", {"start": v(-247.57, 12) * mm, "end": v(-233.43, 12) * mm});
            skLineSegment(sketch, "E289.left", {"start": v(-247.57, 30) * mm, "end": v(-247.57, 12) * mm});
            skLineSegment(sketch, "E289.right", {"start": v(-233.43, 30) * mm, "end": v(-233.43, 12) * mm});
            skLineSegment(sketch, "E290.0", {"start": v(-245.65, 28.07) * mm, "end": v(-241.47, 28.07) * mm});
            skLineSegment(sketch, "E290.1", {"start": v(-245.65, 28.07) * mm, "end": v(-245.65, 21.96) * mm});
            skLineSegment(sketch, "E290.2", {"start": v(-245.65, 13.93) * mm, "end": v(-241.47, 13.93) * mm});
            skLineSegment(sketch, "E290.3", {"start": v(-235.36, 28.07) * mm, "end": v(-235.36, 21.96) * mm});
            skLineSegment(sketch, "E291.left", {"start": v(-241.47, 28.07) * mm, "end": v(-241.47, 21.96) * mm});
            skLineSegment(sketch, "E291.right", {"start": v(-239.54, 28.07) * mm, "end": v(-239.54, 21.96) * mm});
            skLineSegment(sketch, "E292.bottom", {"start": v(-235.36, 21.96) * mm, "end": v(-239.54, 21.96) * mm});
            skLineSegment(sketch, "E292.top", {"start": v(-235.36, 20.04) * mm, "end": v(-239.54, 20.04) * mm});
            skLineSegment(sketch, "E293.trimOffspring", {"start": v(-241.47, 21.96) * mm, "end": v(-245.65, 21.96) * mm});
            skLineSegment(sketch, "E294.trimOffspring", {"start": v(-241.47, 20.04) * mm, "end": v(-241.47, 13.93) * mm});
            skLineSegment(sketch, "E295.trimOffspring", {"start": v(-241.47, 20.04) * mm, "end": v(-245.65, 20.04) * mm});
            skLineSegment(sketch, "E296.trimOffspring", {"start": v(-239.54, 20.04) * mm, "end": v(-239.54, 13.93) * mm});
            skLineSegment(sketch, "E297.trimOffspring", {"start": v(-235.36, 20.04) * mm, "end": v(-235.36, 13.93) * mm});
            skLineSegment(sketch, "E298.trimOffspring", {"start": v(-245.65, 20.04) * mm, "end": v(-245.65, 13.93) * mm});
            skLineSegment(sketch, "E299.trimOffspring", {"start": v(-239.54, 28.07) * mm, "end": v(-235.36, 28.07) * mm});
            skLineSegment(sketch, "E300.trimOffspring", {"start": v(-239.54, 13.93) * mm, "end": v(-235.36, 13.93) * mm});
            skLineSegment(sketch, "E301.left", {"start": v(-233.43, 30.72) * mm, "end": v(-233.43, 12.72) * mm});
            skLineSegment(sketch, "E302.bottom", {"start": v(-183.58, 30) * mm, "end": v(-169.43, 30) * mm});
            skLineSegment(sketch, "E302.top", {"start": v(-183.58, 12) * mm, "end": v(-169.43, 12) * mm});
            skLineSegment(sketch, "E302.left", {"start": v(-183.58, 30) * mm, "end": v(-183.58, 12) * mm});
            skLineSegment(sketch, "E302.right", {"start": v(-169.43, 30) * mm, "end": v(-169.43, 12) * mm});
            skLineSegment(sketch, "E303.0", {"start": v(-181.65, 28.07) * mm, "end": v(-177.47, 28.07) * mm});
            skLineSegment(sketch, "E303.1", {"start": v(-181.65, 28.07) * mm, "end": v(-181.65, 21.96) * mm});
            skLineSegment(sketch, "E303.2", {"start": v(-181.65, 13.93) * mm, "end": v(-177.47, 13.93) * mm});
            skLineSegment(sketch, "E303.3", {"start": v(-171.36, 28.07) * mm, "end": v(-171.36, 21.96) * mm});
            skLineSegment(sketch, "E304.left", {"start": v(-177.47, 28.07) * mm, "end": v(-177.47, 21.96) * mm});
            skLineSegment(sketch, "E304.right", {"start": v(-175.54, 28.07) * mm, "end": v(-175.54, 21.96) * mm});
            skLineSegment(sketch, "E305.bottom", {"start": v(-171.36, 21.96) * mm, "end": v(-175.54, 21.96) * mm});
            skLineSegment(sketch, "E305.top", {"start": v(-171.36, 20.04) * mm, "end": v(-175.54, 20.04) * mm});
            skLineSegment(sketch, "E306.trimOffspring", {"start": v(-177.47, 21.96) * mm, "end": v(-181.65, 21.96) * mm});
            skLineSegment(sketch, "E307.trimOffspring", {"start": v(-177.47, 20.04) * mm, "end": v(-177.47, 13.93) * mm});
            skLineSegment(sketch, "E308.trimOffspring", {"start": v(-177.47, 20.04) * mm, "end": v(-181.65, 20.04) * mm});
            skLineSegment(sketch, "E309.trimOffspring", {"start": v(-175.54, 20.04) * mm, "end": v(-175.54, 13.93) * mm});
            skLineSegment(sketch, "E310.trimOffspring", {"start": v(-171.36, 20.04) * mm, "end": v(-171.36, 13.93) * mm});
            skLineSegment(sketch, "E311.trimOffspring", {"start": v(-181.65, 20.04) * mm, "end": v(-181.65, 13.93) * mm});
            skLineSegment(sketch, "E312.trimOffspring", {"start": v(-175.54, 28.07) * mm, "end": v(-171.36, 28.07) * mm});
            skLineSegment(sketch, "E313.trimOffspring", {"start": v(-175.54, 13.93) * mm, "end": v(-171.36, 13.93) * mm});
            skLineSegment(sketch, "E314.bottom", {"start": v(-151.58, 30) * mm, "end": v(-137.43, 30) * mm});
            skLineSegment(sketch, "E314.top", {"start": v(-151.58, 12) * mm, "end": v(-137.43, 12) * mm});
            skLineSegment(sketch, "E314.left", {"start": v(-151.58, 30) * mm, "end": v(-151.58, 12) * mm});
            skLineSegment(sketch, "E314.right", {"start": v(-137.43, 30) * mm, "end": v(-137.43, 12) * mm});
            skLineSegment(sketch, "E315.0", {"start": v(-149.65, 28.07) * mm, "end": v(-145.47, 28.07) * mm});
            skLineSegment(sketch, "E315.1", {"start": v(-149.65, 28.07) * mm, "end": v(-149.65, 21.96) * mm});
            skLineSegment(sketch, "E315.2", {"start": v(-149.65, 13.93) * mm, "end": v(-145.47, 13.93) * mm});
            skLineSegment(sketch, "E315.3", {"start": v(-139.36, 28.07) * mm, "end": v(-139.36, 21.96) * mm});
            skLineSegment(sketch, "E316.left", {"start": v(-145.47, 28.07) * mm, "end": v(-145.47, 21.96) * mm});
            skLineSegment(sketch, "E316.right", {"start": v(-143.54, 28.07) * mm, "end": v(-143.54, 21.96) * mm});
            skLineSegment(sketch, "E317.bottom", {"start": v(-139.36, 21.96) * mm, "end": v(-143.54, 21.96) * mm});
            skLineSegment(sketch, "E317.top", {"start": v(-139.36, 20.04) * mm, "end": v(-143.54, 20.04) * mm});
            skLineSegment(sketch, "E318.trimOffspring", {"start": v(-145.47, 21.96) * mm, "end": v(-149.65, 21.96) * mm});
            skLineSegment(sketch, "E319.trimOffspring", {"start": v(-145.47, 20.04) * mm, "end": v(-145.47, 13.93) * mm});
            skLineSegment(sketch, "E320.trimOffspring", {"start": v(-145.47, 20.04) * mm, "end": v(-149.65, 20.04) * mm});
            skLineSegment(sketch, "E321.trimOffspring", {"start": v(-143.54, 20.04) * mm, "end": v(-143.54, 13.93) * mm});
            skLineSegment(sketch, "E322.trimOffspring", {"start": v(-139.36, 20.04) * mm, "end": v(-139.36, 13.93) * mm});
            skLineSegment(sketch, "E323.trimOffspring", {"start": v(-149.65, 20.04) * mm, "end": v(-149.65, 13.93) * mm});
            skLineSegment(sketch, "E324.trimOffspring", {"start": v(-143.54, 28.07) * mm, "end": v(-139.36, 28.07) * mm});
            skLineSegment(sketch, "E325.trimOffspring", {"start": v(-143.54, 13.93) * mm, "end": v(-139.36, 13.93) * mm});
            skLineSegment(sketch, "E326.left", {"start": v(-137.43, 30) * mm, "end": v(-137.43, 18.3) * mm});
            skSolve(sketch);
        }
        {
            var Q0;
            Q0 = qSketchRegion(id + "F39", true);
            extrude(context, id + "F40", {"entities" : qUnion([Q0]), "operationType" : NewBodyOperationType.REMOVE, "oppositeDirection" : true, "depth" : .5 * mm, "offsetDistance" : 25 * mm});
        }
        {
            var Q0;
            {var subQ7=sQuery(id+"F0.wireOp",EDGE,"E4");Q0=makeQuery(id+"F16.boolean.opBoolean","SPLIT",FACE,{"disambiguationData":[TD([makeQuery(id+"F16.opExtrude","SWEPT_FACE",FACE,{"disambiguationData":[OSD([sQuery(id+"F8.wireOp",EDGE,"E63.6.0.0")])]})])],"derivedFrom":makeQuery(id+"F1.opExtrude","SWEPT_FACE",FACE,{"disambiguationData":[OSD([subQ7])]})});}
            var sketch = newSketch(context, id + "F41", { "sketchPlane" : qUnion([Q0])});
            skLineSegment(sketch, "E327.bottom", {"start": v(41.3, 30) * mm, "end": v(55.44, 30) * mm});
            skLineSegment(sketch, "E327.top", {"start": v(41.3, 12) * mm, "end": v(55.44, 12) * mm});
            skLineSegment(sketch, "E327.left", {"start": v(41.3, 30) * mm, "end": v(41.3, 12) * mm});
            skLineSegment(sketch, "E327.right", {"start": v(55.44, 30) * mm, "end": v(55.44, 12) * mm});
            skLineSegment(sketch, "E328.0", {"start": v(43.23, 28.07) * mm, "end": v(47.4, 28.07) * mm});
            skLineSegment(sketch, "E328.1", {"start": v(43.23, 28.07) * mm, "end": v(43.23, 21.96) * mm});
            skLineSegment(sketch, "E328.2", {"start": v(43.23, 13.93) * mm, "end": v(47.4, 13.93) * mm});
            skLineSegment(sketch, "E328.3", {"start": v(53.51, 28.07) * mm, "end": v(53.51, 21.96) * mm});
            skLineSegment(sketch, "E329.left", {"start": v(47.4, 28.07) * mm, "end": v(47.4, 21.96) * mm});
            skLineSegment(sketch, "E329.right", {"start": v(49.34, 28.07) * mm, "end": v(49.34, 21.96) * mm});
            skLineSegment(sketch, "E330.bottom", {"start": v(53.51, 21.96) * mm, "end": v(49.34, 21.96) * mm});
            skLineSegment(sketch, "E330.top", {"start": v(53.51, 20.04) * mm, "end": v(49.34, 20.04) * mm});
            skLineSegment(sketch, "E331.trimOffspring", {"start": v(47.4, 21.96) * mm, "end": v(43.23, 21.96) * mm});
            skLineSegment(sketch, "E332.trimOffspring", {"start": v(47.4, 20.04) * mm, "end": v(47.4, 13.93) * mm});
            skLineSegment(sketch, "E333.trimOffspring", {"start": v(47.4, 20.04) * mm, "end": v(43.23, 20.04) * mm});
            skLineSegment(sketch, "E334.trimOffspring", {"start": v(49.34, 20.04) * mm, "end": v(49.34, 13.93) * mm});
            skLineSegment(sketch, "E335.trimOffspring", {"start": v(53.51, 20.04) * mm, "end": v(53.51, 13.93) * mm});
            skLineSegment(sketch, "E336.trimOffspring", {"start": v(43.23, 20.04) * mm, "end": v(43.23, 13.93) * mm});
            skLineSegment(sketch, "E337.trimOffspring", {"start": v(49.34, 28.07) * mm, "end": v(53.51, 28.07) * mm});
            skLineSegment(sketch, "E338.trimOffspring", {"start": v(49.34, 13.93) * mm, "end": v(53.51, 13.93) * mm});
            skLineSegment(sketch, "E339.bottom", {"start": v(73.3, 30) * mm, "end": v(87.44, 30) * mm});
            skLineSegment(sketch, "E339.top", {"start": v(73.3, 12) * mm, "end": v(87.44, 12) * mm});
            skLineSegment(sketch, "E339.left", {"start": v(73.3, 30) * mm, "end": v(73.3, 12) * mm});
            skLineSegment(sketch, "E339.right", {"start": v(87.44, 30) * mm, "end": v(87.44, 12) * mm});
            skLineSegment(sketch, "E340.0", {"start": v(75.23, 28.07) * mm, "end": v(79.4, 28.07) * mm});
            skLineSegment(sketch, "E340.1", {"start": v(75.23, 28.07) * mm, "end": v(75.23, 21.96) * mm});
            skLineSegment(sketch, "E340.2", {"start": v(75.23, 13.93) * mm, "end": v(79.4, 13.93) * mm});
            skLineSegment(sketch, "E340.3", {"start": v(85.51, 28.07) * mm, "end": v(85.51, 21.96) * mm});
            skLineSegment(sketch, "E341.left", {"start": v(79.4, 28.07) * mm, "end": v(79.4, 21.96) * mm});
            skLineSegment(sketch, "E341.right", {"start": v(81.34, 28.07) * mm, "end": v(81.34, 21.96) * mm});
            skLineSegment(sketch, "E342.bottom", {"start": v(85.51, 21.96) * mm, "end": v(81.34, 21.96) * mm});
            skLineSegment(sketch, "E342.top", {"start": v(85.51, 20.04) * mm, "end": v(81.34, 20.04) * mm});
            skLineSegment(sketch, "E343.trimOffspring", {"start": v(79.4, 21.96) * mm, "end": v(75.23, 21.96) * mm});
            skLineSegment(sketch, "E344.trimOffspring", {"start": v(79.4, 20.04) * mm, "end": v(79.4, 13.93) * mm});
            skLineSegment(sketch, "E345.trimOffspring", {"start": v(79.4, 20.04) * mm, "end": v(75.23, 20.04) * mm});
            skLineSegment(sketch, "E346.trimOffspring", {"start": v(81.34, 20.04) * mm, "end": v(81.34, 13.93) * mm});
            skLineSegment(sketch, "E347.trimOffspring", {"start": v(85.51, 20.04) * mm, "end": v(85.51, 13.93) * mm});
            skLineSegment(sketch, "E348.trimOffspring", {"start": v(75.23, 20.04) * mm, "end": v(75.23, 13.93) * mm});
            skLineSegment(sketch, "E349.trimOffspring", {"start": v(81.34, 28.07) * mm, "end": v(85.51, 28.07) * mm});
            skLineSegment(sketch, "E350.trimOffspring", {"start": v(81.34, 13.93) * mm, "end": v(85.51, 13.93) * mm});
            skLineSegment(sketch, "E351.bottom", {"start": v(105.3, 30) * mm, "end": v(119.44, 30) * mm});
            skLineSegment(sketch, "E351.top", {"start": v(105.3, 12) * mm, "end": v(119.44, 12) * mm});
            skLineSegment(sketch, "E351.left", {"start": v(105.3, 30) * mm, "end": v(105.3, 12) * mm});
            skLineSegment(sketch, "E351.right", {"start": v(119.44, 30) * mm, "end": v(119.44, 12) * mm});
            skLineSegment(sketch, "E352.0", {"start": v(107.23, 28.07) * mm, "end": v(111.4, 28.07) * mm});
            skLineSegment(sketch, "E352.1", {"start": v(107.23, 28.07) * mm, "end": v(107.23, 21.96) * mm});
            skLineSegment(sketch, "E352.2", {"start": v(107.23, 13.93) * mm, "end": v(111.4, 13.93) * mm});
            skLineSegment(sketch, "E352.3", {"start": v(117.51, 28.07) * mm, "end": v(117.51, 21.96) * mm});
            skLineSegment(sketch, "E353.left", {"start": v(111.4, 28.07) * mm, "end": v(111.4, 21.96) * mm});
            skLineSegment(sketch, "E353.right", {"start": v(113.34, 28.07) * mm, "end": v(113.34, 21.96) * mm});
            skLineSegment(sketch, "E354.bottom", {"start": v(117.51, 21.96) * mm, "end": v(113.34, 21.96) * mm});
            skLineSegment(sketch, "E354.top", {"start": v(117.51, 20.04) * mm, "end": v(113.34, 20.04) * mm});
            skLineSegment(sketch, "E355.trimOffspring", {"start": v(111.4, 21.96) * mm, "end": v(107.23, 21.96) * mm});
            skLineSegment(sketch, "E356.trimOffspring", {"start": v(111.4, 20.04) * mm, "end": v(111.4, 13.93) * mm});
            skLineSegment(sketch, "E357.trimOffspring", {"start": v(111.4, 20.04) * mm, "end": v(107.23, 20.04) * mm});
            skLineSegment(sketch, "E358.trimOffspring", {"start": v(113.34, 20.04) * mm, "end": v(113.34, 13.93) * mm});
            skLineSegment(sketch, "E359.trimOffspring", {"start": v(117.51, 20.04) * mm, "end": v(117.51, 13.93) * mm});
            skLineSegment(sketch, "E360.trimOffspring", {"start": v(107.23, 20.04) * mm, "end": v(107.23, 13.93) * mm});
            skLineSegment(sketch, "E361.trimOffspring", {"start": v(113.34, 28.07) * mm, "end": v(117.51, 28.07) * mm});
            skLineSegment(sketch, "E362.trimOffspring", {"start": v(113.34, 13.93) * mm, "end": v(117.51, 13.93) * mm});
            skLineSegment(sketch, "E363.bottom", {"start": v(137.3, 30) * mm, "end": v(151.44, 30) * mm});
            skLineSegment(sketch, "E363.top", {"start": v(137.3, 12) * mm, "end": v(151.44, 12) * mm});
            skLineSegment(sketch, "E363.left", {"start": v(137.3, 30) * mm, "end": v(137.3, 12) * mm});
            skLineSegment(sketch, "E363.right", {"start": v(151.44, 30) * mm, "end": v(151.44, 12) * mm});
            skLineSegment(sketch, "E364.0", {"start": v(139.23, 28.07) * mm, "end": v(143.4, 28.07) * mm});
            skLineSegment(sketch, "E364.1", {"start": v(139.23, 28.07) * mm, "end": v(139.23, 21.96) * mm});
            skLineSegment(sketch, "E364.2", {"start": v(139.23, 13.93) * mm, "end": v(143.4, 13.93) * mm});
            skLineSegment(sketch, "E364.3", {"start": v(149.51, 28.07) * mm, "end": v(149.51, 21.96) * mm});
            skLineSegment(sketch, "E365.left", {"start": v(143.4, 28.07) * mm, "end": v(143.4, 21.96) * mm});
            skLineSegment(sketch, "E365.right", {"start": v(145.34, 28.07) * mm, "end": v(145.34, 21.96) * mm});
            skLineSegment(sketch, "E366.bottom", {"start": v(149.51, 21.96) * mm, "end": v(145.34, 21.96) * mm});
            skLineSegment(sketch, "E366.top", {"start": v(149.51, 20.04) * mm, "end": v(145.34, 20.04) * mm});
            skLineSegment(sketch, "E367.trimOffspring", {"start": v(143.4, 21.96) * mm, "end": v(139.23, 21.96) * mm});
            skLineSegment(sketch, "E368.trimOffspring", {"start": v(143.4, 20.04) * mm, "end": v(143.4, 13.93) * mm});
            skLineSegment(sketch, "E369.trimOffspring", {"start": v(143.4, 20.04) * mm, "end": v(139.23, 20.04) * mm});
            skLineSegment(sketch, "E370.trimOffspring", {"start": v(145.34, 20.04) * mm, "end": v(145.34, 13.93) * mm});
            skLineSegment(sketch, "E371.trimOffspring", {"start": v(149.51, 20.04) * mm, "end": v(149.51, 13.93) * mm});
            skLineSegment(sketch, "E372.trimOffspring", {"start": v(139.23, 20.04) * mm, "end": v(139.23, 13.93) * mm});
            skLineSegment(sketch, "E373.trimOffspring", {"start": v(145.34, 28.07) * mm, "end": v(149.51, 28.07) * mm});
            skLineSegment(sketch, "E374.trimOffspring", {"start": v(145.34, 13.93) * mm, "end": v(149.51, 13.93) * mm});
            skLineSegment(sketch, "E375.bottom", {"start": v(169.3, 30) * mm, "end": v(183.44, 30) * mm});
            skLineSegment(sketch, "E375.top", {"start": v(169.3, 12) * mm, "end": v(183.44, 12) * mm});
            skLineSegment(sketch, "E375.left", {"start": v(169.3, 30) * mm, "end": v(169.3, 12) * mm});
            skLineSegment(sketch, "E375.right", {"start": v(183.44, 30) * mm, "end": v(183.44, 12) * mm});
            skLineSegment(sketch, "E376.0", {"start": v(171.23, 28.07) * mm, "end": v(175.4, 28.07) * mm});
            skLineSegment(sketch, "E376.1", {"start": v(171.23, 28.07) * mm, "end": v(171.23, 21.96) * mm});
            skLineSegment(sketch, "E376.2", {"start": v(171.23, 13.93) * mm, "end": v(175.4, 13.93) * mm});
            skLineSegment(sketch, "E376.3", {"start": v(181.51, 28.07) * mm, "end": v(181.51, 21.96) * mm});
            skLineSegment(sketch, "E377.left", {"start": v(175.4, 28.07) * mm, "end": v(175.4, 21.96) * mm});
            skLineSegment(sketch, "E377.right", {"start": v(177.34, 28.07) * mm, "end": v(177.34, 21.96) * mm});
            skLineSegment(sketch, "E378.bottom", {"start": v(181.51, 21.96) * mm, "end": v(177.34, 21.96) * mm});
            skLineSegment(sketch, "E378.top", {"start": v(181.51, 20.04) * mm, "end": v(177.34, 20.04) * mm});
            skLineSegment(sketch, "E379.trimOffspring", {"start": v(175.4, 21.96) * mm, "end": v(171.23, 21.96) * mm});
            skLineSegment(sketch, "E380.trimOffspring", {"start": v(175.4, 20.04) * mm, "end": v(175.4, 13.93) * mm});
            skLineSegment(sketch, "E381.trimOffspring", {"start": v(175.4, 20.04) * mm, "end": v(171.23, 20.04) * mm});
            skLineSegment(sketch, "E382.trimOffspring", {"start": v(177.34, 20.04) * mm, "end": v(177.34, 13.93) * mm});
            skLineSegment(sketch, "E383.trimOffspring", {"start": v(181.51, 20.04) * mm, "end": v(181.51, 13.93) * mm});
            skLineSegment(sketch, "E384.trimOffspring", {"start": v(171.23, 20.04) * mm, "end": v(171.23, 13.93) * mm});
            skLineSegment(sketch, "E385.trimOffspring", {"start": v(177.34, 28.07) * mm, "end": v(181.51, 28.07) * mm});
            skLineSegment(sketch, "E386.trimOffspring", {"start": v(177.34, 13.93) * mm, "end": v(181.51, 13.93) * mm});
            skLineSegment(sketch, "E387.bottom", {"start": v(201.3, 30) * mm, "end": v(215.44, 30) * mm});
            skLineSegment(sketch, "E387.top", {"start": v(201.3, 12) * mm, "end": v(215.44, 12) * mm});
            skLineSegment(sketch, "E387.left", {"start": v(201.3, 30) * mm, "end": v(201.3, 12) * mm});
            skLineSegment(sketch, "E387.right", {"start": v(215.44, 30) * mm, "end": v(215.44, 12) * mm});
            skLineSegment(sketch, "E388.0", {"start": v(203.23, 28.07) * mm, "end": v(207.4, 28.07) * mm});
            skLineSegment(sketch, "E388.1", {"start": v(203.23, 28.07) * mm, "end": v(203.23, 21.96) * mm});
            skLineSegment(sketch, "E388.2", {"start": v(203.23, 13.93) * mm, "end": v(207.4, 13.93) * mm});
            skLineSegment(sketch, "E388.3", {"start": v(213.51, 28.07) * mm, "end": v(213.51, 21.96) * mm});
            skLineSegment(sketch, "E389.left", {"start": v(207.4, 28.07) * mm, "end": v(207.4, 21.96) * mm});
            skLineSegment(sketch, "E389.right", {"start": v(209.34, 28.07) * mm, "end": v(209.34, 21.96) * mm});
            skLineSegment(sketch, "E390.bottom", {"start": v(213.51, 21.96) * mm, "end": v(209.34, 21.96) * mm});
            skLineSegment(sketch, "E390.top", {"start": v(213.51, 20.04) * mm, "end": v(209.34, 20.04) * mm});
            skLineSegment(sketch, "E391.trimOffspring", {"start": v(207.4, 21.96) * mm, "end": v(203.23, 21.96) * mm});
            skLineSegment(sketch, "E392.trimOffspring", {"start": v(207.4, 20.04) * mm, "end": v(207.4, 13.93) * mm});
            skLineSegment(sketch, "E393.trimOffspring", {"start": v(207.4, 20.04) * mm, "end": v(203.23, 20.04) * mm});
            skLineSegment(sketch, "E394.trimOffspring", {"start": v(209.34, 20.04) * mm, "end": v(209.34, 13.93) * mm});
            skLineSegment(sketch, "E395.trimOffspring", {"start": v(213.51, 20.04) * mm, "end": v(213.51, 13.93) * mm});
            skLineSegment(sketch, "E396.trimOffspring", {"start": v(203.23, 20.04) * mm, "end": v(203.23, 13.93) * mm});
            skLineSegment(sketch, "E397.trimOffspring", {"start": v(209.34, 28.07) * mm, "end": v(213.51, 28.07) * mm});
            skLineSegment(sketch, "E398.trimOffspring", {"start": v(209.34, 13.93) * mm, "end": v(213.51, 13.93) * mm});
            skLineSegment(sketch, "E399.left", {"start": v(215.44, 31.5) * mm, "end": v(215.44, 13.5) * mm});
            skSolve(sketch);
        }
        {
            var Q0;
            Q0 = qSketchRegion(id + "F41", true);
            extrude(context, id + "F42", {"entities" : qUnion([Q0]), "operationType" : NewBodyOperationType.REMOVE, "oppositeDirection" : true, "depth" : .5 * mm, "offsetDistance" : 25 * mm});
        }
        {
            var Q0;
            {var subQ5=sQuery(id+"F0.wireOp",EDGE,"E6");Q0=makeQuery(id+"F19.boolean.opBoolean","SPLIT",FACE,{"disambiguationData":[TD([makeQuery(id+"F19.opExtrude","SWEPT_FACE",FACE,{"disambiguationData":[OSD([sQuery(id+"F15.wireOp",EDGE,"E122.1.0.0")])]})])],"derivedFrom":makeQuery(id+"F1.opExtrude","SWEPT_FACE",FACE,{"disambiguationData":[OSD([subQ5])]})});}
            var sketch = newSketch(context, id + "F43", { "sketchPlane" : qUnion([Q0])});
            skLineSegment(sketch, "E400.bottom", {"start": v(-215.7, 30) * mm, "end": v(-201.56, 30) * mm});
            skLineSegment(sketch, "E400.top", {"start": v(-215.7, 12) * mm, "end": v(-201.56, 12) * mm});
            skLineSegment(sketch, "E400.left", {"start": v(-215.7, 30) * mm, "end": v(-215.7, 12) * mm});
            skLineSegment(sketch, "E400.right", {"start": v(-201.56, 30) * mm, "end": v(-201.56, 12) * mm});
            skLineSegment(sketch, "E401.0", {"start": v(-213.77, 28.07) * mm, "end": v(-209.6, 28.07) * mm});
            skLineSegment(sketch, "E401.1", {"start": v(-213.77, 28.07) * mm, "end": v(-213.77, 21.96) * mm});
            skLineSegment(sketch, "E401.2", {"start": v(-213.77, 13.93) * mm, "end": v(-209.6, 13.93) * mm});
            skLineSegment(sketch, "E401.3", {"start": v(-203.49, 28.07) * mm, "end": v(-203.49, 21.96) * mm});
            skLineSegment(sketch, "E402.left", {"start": v(-209.6, 28.07) * mm, "end": v(-209.6, 21.96) * mm});
            skLineSegment(sketch, "E402.right", {"start": v(-207.66, 28.07) * mm, "end": v(-207.66, 21.96) * mm});
            skLineSegment(sketch, "E403.bottom", {"start": v(-203.49, 21.96) * mm, "end": v(-207.66, 21.96) * mm});
            skLineSegment(sketch, "E403.top", {"start": v(-203.49, 20.04) * mm, "end": v(-207.66, 20.04) * mm});
            skLineSegment(sketch, "E404.trimOffspring", {"start": v(-209.6, 21.96) * mm, "end": v(-213.77, 21.96) * mm});
            skLineSegment(sketch, "E405.trimOffspring", {"start": v(-209.6, 20.04) * mm, "end": v(-209.6, 13.93) * mm});
            skLineSegment(sketch, "E406.trimOffspring", {"start": v(-209.6, 20.04) * mm, "end": v(-213.77, 20.04) * mm});
            skLineSegment(sketch, "E407.trimOffspring", {"start": v(-207.66, 20.04) * mm, "end": v(-207.66, 13.93) * mm});
            skLineSegment(sketch, "E408.trimOffspring", {"start": v(-203.49, 20.04) * mm, "end": v(-203.49, 13.93) * mm});
            skLineSegment(sketch, "E409.trimOffspring", {"start": v(-213.77, 20.04) * mm, "end": v(-213.77, 13.93) * mm});
            skLineSegment(sketch, "E410.trimOffspring", {"start": v(-207.66, 28.07) * mm, "end": v(-203.49, 28.07) * mm});
            skLineSegment(sketch, "E411.trimOffspring", {"start": v(-207.66, 13.93) * mm, "end": v(-203.49, 13.93) * mm});
            skLineSegment(sketch, "E412.bottom", {"start": v(-183.7, 30) * mm, "end": v(-169.56, 30) * mm});
            skLineSegment(sketch, "E412.top", {"start": v(-183.7, 12) * mm, "end": v(-169.56, 12) * mm});
            skLineSegment(sketch, "E412.left", {"start": v(-183.7, 30) * mm, "end": v(-183.7, 12) * mm});
            skLineSegment(sketch, "E412.right", {"start": v(-169.56, 30) * mm, "end": v(-169.56, 12) * mm});
            skLineSegment(sketch, "E413.0", {"start": v(-181.77, 28.07) * mm, "end": v(-177.6, 28.07) * mm});
            skLineSegment(sketch, "E413.1", {"start": v(-181.77, 28.07) * mm, "end": v(-181.77, 21.96) * mm});
            skLineSegment(sketch, "E413.2", {"start": v(-181.77, 13.93) * mm, "end": v(-177.6, 13.93) * mm});
            skLineSegment(sketch, "E413.3", {"start": v(-171.49, 28.07) * mm, "end": v(-171.49, 21.96) * mm});
            skLineSegment(sketch, "E414.left", {"start": v(-177.6, 28.07) * mm, "end": v(-177.6, 21.96) * mm});
            skLineSegment(sketch, "E414.right", {"start": v(-175.66, 28.07) * mm, "end": v(-175.66, 21.96) * mm});
            skLineSegment(sketch, "E415.bottom", {"start": v(-171.49, 21.96) * mm, "end": v(-175.66, 21.96) * mm});
            skLineSegment(sketch, "E415.top", {"start": v(-171.49, 20.04) * mm, "end": v(-175.66, 20.04) * mm});
            skLineSegment(sketch, "E416.trimOffspring", {"start": v(-177.6, 21.96) * mm, "end": v(-181.77, 21.96) * mm});
            skLineSegment(sketch, "E417.trimOffspring", {"start": v(-177.6, 20.04) * mm, "end": v(-177.6, 13.93) * mm});
            skLineSegment(sketch, "E418.trimOffspring", {"start": v(-177.6, 20.04) * mm, "end": v(-181.77, 20.04) * mm});
            skLineSegment(sketch, "E419.trimOffspring", {"start": v(-175.66, 20.04) * mm, "end": v(-175.66, 13.93) * mm});
            skLineSegment(sketch, "E420.trimOffspring", {"start": v(-171.49, 20.04) * mm, "end": v(-171.49, 13.93) * mm});
            skLineSegment(sketch, "E421.trimOffspring", {"start": v(-181.77, 20.04) * mm, "end": v(-181.77, 13.93) * mm});
            skLineSegment(sketch, "E422.trimOffspring", {"start": v(-175.66, 28.07) * mm, "end": v(-171.49, 28.07) * mm});
            skLineSegment(sketch, "E423.trimOffspring", {"start": v(-175.66, 13.93) * mm, "end": v(-171.49, 13.93) * mm});
            skLineSegment(sketch, "E424.bottom", {"start": v(-151.7, 30) * mm, "end": v(-137.56, 30) * mm});
            skLineSegment(sketch, "E424.top", {"start": v(-151.7, 12) * mm, "end": v(-137.56, 12) * mm});
            skLineSegment(sketch, "E424.left", {"start": v(-151.7, 30) * mm, "end": v(-151.7, 12) * mm});
            skLineSegment(sketch, "E424.right", {"start": v(-137.56, 30) * mm, "end": v(-137.56, 12) * mm});
            skLineSegment(sketch, "E425.0", {"start": v(-149.77, 28.07) * mm, "end": v(-145.6, 28.07) * mm});
            skLineSegment(sketch, "E425.1", {"start": v(-149.77, 28.07) * mm, "end": v(-149.77, 21.96) * mm});
            skLineSegment(sketch, "E425.2", {"start": v(-149.77, 13.93) * mm, "end": v(-145.6, 13.93) * mm});
            skLineSegment(sketch, "E425.3", {"start": v(-139.49, 28.07) * mm, "end": v(-139.49, 21.96) * mm});
            skLineSegment(sketch, "E426.left", {"start": v(-145.6, 28.07) * mm, "end": v(-145.6, 21.96) * mm});
            skLineSegment(sketch, "E426.right", {"start": v(-143.66, 28.07) * mm, "end": v(-143.66, 21.96) * mm});
            skLineSegment(sketch, "E427.bottom", {"start": v(-139.49, 21.96) * mm, "end": v(-143.66, 21.96) * mm});
            skLineSegment(sketch, "E427.top", {"start": v(-139.49, 20.04) * mm, "end": v(-143.66, 20.04) * mm});
            skLineSegment(sketch, "E428.trimOffspring", {"start": v(-145.6, 21.96) * mm, "end": v(-149.77, 21.96) * mm});
            skLineSegment(sketch, "E429.trimOffspring", {"start": v(-145.6, 20.04) * mm, "end": v(-145.6, 13.93) * mm});
            skLineSegment(sketch, "E430.trimOffspring", {"start": v(-145.6, 20.04) * mm, "end": v(-149.77, 20.04) * mm});
            skLineSegment(sketch, "E431.trimOffspring", {"start": v(-143.66, 20.04) * mm, "end": v(-143.66, 13.93) * mm});
            skLineSegment(sketch, "E432.trimOffspring", {"start": v(-139.49, 20.04) * mm, "end": v(-139.49, 13.93) * mm});
            skLineSegment(sketch, "E433.trimOffspring", {"start": v(-149.77, 20.04) * mm, "end": v(-149.77, 13.93) * mm});
            skLineSegment(sketch, "E434.trimOffspring", {"start": v(-143.66, 28.07) * mm, "end": v(-139.49, 28.07) * mm});
            skLineSegment(sketch, "E435.trimOffspring", {"start": v(-143.66, 13.93) * mm, "end": v(-139.49, 13.93) * mm});
            skLineSegment(sketch, "E436.left", {"start": v(-137.56, 30.15) * mm, "end": v(-137.56, 12.15) * mm});
            skLineSegment(sketch, "E437.bottom", {"start": v(-119.7, 30) * mm, "end": v(-105.56, 30) * mm});
            skLineSegment(sketch, "E437.top", {"start": v(-119.7, 12) * mm, "end": v(-105.56, 12) * mm});
            skLineSegment(sketch, "E437.left", {"start": v(-119.7, 30) * mm, "end": v(-119.7, 12) * mm});
            skLineSegment(sketch, "E437.right", {"start": v(-105.56, 30) * mm, "end": v(-105.56, 12) * mm});
            skLineSegment(sketch, "E438.0", {"start": v(-117.77, 28.07) * mm, "end": v(-113.6, 28.07) * mm});
            skLineSegment(sketch, "E438.1", {"start": v(-117.77, 28.07) * mm, "end": v(-117.77, 21.96) * mm});
            skLineSegment(sketch, "E438.2", {"start": v(-117.77, 13.93) * mm, "end": v(-113.6, 13.93) * mm});
            skLineSegment(sketch, "E438.3", {"start": v(-107.49, 28.07) * mm, "end": v(-107.49, 21.96) * mm});
            skLineSegment(sketch, "E439.left", {"start": v(-113.6, 28.07) * mm, "end": v(-113.6, 21.96) * mm});
            skLineSegment(sketch, "E439.right", {"start": v(-111.66, 28.07) * mm, "end": v(-111.66, 21.96) * mm});
            skLineSegment(sketch, "E440.bottom", {"start": v(-107.49, 21.96) * mm, "end": v(-111.66, 21.96) * mm});
            skLineSegment(sketch, "E440.top", {"start": v(-107.49, 20.04) * mm, "end": v(-111.66, 20.04) * mm});
            skLineSegment(sketch, "E441.trimOffspring", {"start": v(-113.6, 21.96) * mm, "end": v(-117.77, 21.96) * mm});
            skLineSegment(sketch, "E442.trimOffspring", {"start": v(-113.6, 20.04) * mm, "end": v(-113.6, 13.93) * mm});
            skLineSegment(sketch, "E443.trimOffspring", {"start": v(-113.6, 20.04) * mm, "end": v(-117.77, 20.04) * mm});
            skLineSegment(sketch, "E444.trimOffspring", {"start": v(-111.66, 20.04) * mm, "end": v(-111.66, 13.93) * mm});
            skLineSegment(sketch, "E445.trimOffspring", {"start": v(-107.49, 20.04) * mm, "end": v(-107.49, 13.93) * mm});
            skLineSegment(sketch, "E446.trimOffspring", {"start": v(-117.77, 20.04) * mm, "end": v(-117.77, 13.93) * mm});
            skLineSegment(sketch, "E447.trimOffspring", {"start": v(-111.66, 28.07) * mm, "end": v(-107.49, 28.07) * mm});
            skLineSegment(sketch, "E448.trimOffspring", {"start": v(-111.66, 13.93) * mm, "end": v(-107.49, 13.93) * mm});
            skLineSegment(sketch, "E449.left", {"start": v(-105.56, 31.3) * mm, "end": v(-105.56, 13.3) * mm});
            skLineSegment(sketch, "E450.bottom", {"start": v(-87.7, 30) * mm, "end": v(-73.56, 30) * mm});
            skLineSegment(sketch, "E450.top", {"start": v(-87.7, 12) * mm, "end": v(-73.56, 12) * mm});
            skLineSegment(sketch, "E450.left", {"start": v(-87.7, 30) * mm, "end": v(-87.7, 12) * mm});
            skLineSegment(sketch, "E450.right", {"start": v(-73.56, 30) * mm, "end": v(-73.56, 12) * mm});
            skLineSegment(sketch, "E451.0", {"start": v(-85.77, 28.07) * mm, "end": v(-81.6, 28.07) * mm});
            skLineSegment(sketch, "E451.1", {"start": v(-85.77, 28.07) * mm, "end": v(-85.77, 21.96) * mm});
            skLineSegment(sketch, "E451.2", {"start": v(-85.77, 13.93) * mm, "end": v(-81.6, 13.93) * mm});
            skLineSegment(sketch, "E451.3", {"start": v(-75.49, 28.07) * mm, "end": v(-75.49, 21.96) * mm});
            skLineSegment(sketch, "E452.left", {"start": v(-81.6, 28.07) * mm, "end": v(-81.6, 21.96) * mm});
            skLineSegment(sketch, "E452.right", {"start": v(-79.66, 28.07) * mm, "end": v(-79.66, 21.96) * mm});
            skLineSegment(sketch, "E453.bottom", {"start": v(-75.49, 21.96) * mm, "end": v(-79.66, 21.96) * mm});
            skLineSegment(sketch, "E453.top", {"start": v(-75.49, 20.04) * mm, "end": v(-79.66, 20.04) * mm});
            skLineSegment(sketch, "E454.trimOffspring", {"start": v(-81.6, 21.96) * mm, "end": v(-85.77, 21.96) * mm});
            skLineSegment(sketch, "E455.trimOffspring", {"start": v(-81.6, 20.04) * mm, "end": v(-81.6, 13.93) * mm});
            skLineSegment(sketch, "E456.trimOffspring", {"start": v(-81.6, 20.04) * mm, "end": v(-85.77, 20.04) * mm});
            skLineSegment(sketch, "E457.trimOffspring", {"start": v(-79.66, 20.04) * mm, "end": v(-79.66, 13.93) * mm});
            skLineSegment(sketch, "E458.trimOffspring", {"start": v(-75.49, 20.04) * mm, "end": v(-75.49, 13.93) * mm});
            skLineSegment(sketch, "E459.trimOffspring", {"start": v(-85.77, 20.04) * mm, "end": v(-85.77, 13.93) * mm});
            skLineSegment(sketch, "E460.trimOffspring", {"start": v(-79.66, 28.07) * mm, "end": v(-75.49, 28.07) * mm});
            skLineSegment(sketch, "E461.trimOffspring", {"start": v(-79.66, 13.93) * mm, "end": v(-75.49, 13.93) * mm});
            skLineSegment(sketch, "E462.left", {"start": v(-73.56, 31.52) * mm, "end": v(-73.56, 13.52) * mm});
            skSolve(sketch);
        }
        {
            var Q0;
            Q0 = qSketchRegion(id + "F43", true);
            extrude(context, id + "F44", {"entities" : qUnion([Q0]), "operationType" : NewBodyOperationType.REMOVE, "oppositeDirection" : true, "depth" : .5 * mm, "offsetDistance" : 25 * mm});
        }
    });
